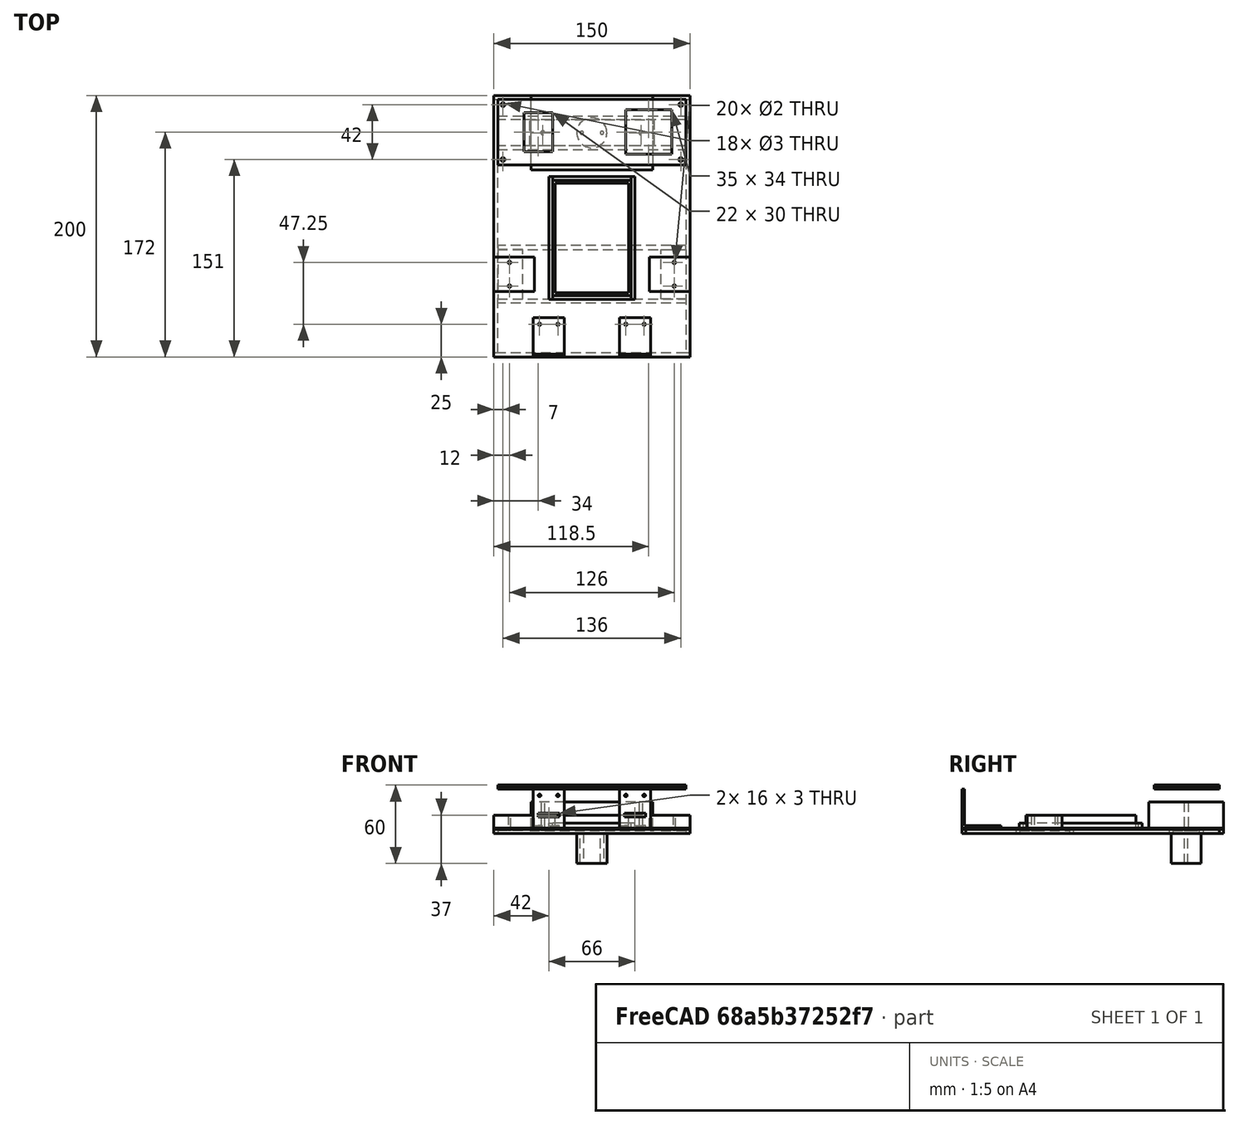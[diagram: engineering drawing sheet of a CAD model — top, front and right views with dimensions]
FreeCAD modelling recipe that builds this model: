
FCSTD DOCUMENT  (FreeCAD 0.20R27078 (Git))
Label: Robot_simple_brackets
License: All rights reserved
LicenseURL: http://en.wikipedia.org/wiki/All_rights_reserved
objects: TechDraw::DrawViewDimension×63, PartDesign::ShapeBinder×32, PartDesign::Pad×27, PartDesign::Body×25, TechDraw::DrawProjGroupItem×13, Sketcher::SketchObject×11, TechDraw::DrawProjGroup×10, PartDesign::Pocket×7, TechDraw::DrawSVGTemplate×5, TechDraw::DrawPage×5, PartDesign::Fillet×2, TechDraw::DrawViewAnnotation×2, TechDraw::DrawHatch×1, App::DocumentObjectGroup×1
note: 140 computed .brp shape members not serialized (recipe doc carries the construction recipe); baked Part::Feature solids carry a one-line shape summary decoded from their .brp

FEATURE [Sketcher::SketchObject] Sketch  label="ChassisOutline"
  FullyConstrained = true
  MapMode = 5
  Support = -> [XY_Plane]
  sketch-geometry (4):
    g0: LineSegment StartX=-75 StartY=100 StartZ=0 EndX=75 EndY=100 EndZ=0
    g1: LineSegment StartX=75 StartY=100 StartZ=0 EndX=75 EndY=-100 EndZ=0
    g2: LineSegment StartX=75 StartY=-100 StartZ=0 EndX=-75 EndY=-100 EndZ=0
    g3: LineSegment StartX=-75 StartY=-100 StartZ=0 EndX=-75 EndY=100 EndZ=0
  constraints (11):
    c: Coincident(g0,g1)
    c: Coincident(g1,g2)
    c: Coincident(g2,g3)
    c: Coincident(g3,g0)
    c: Horizontal(g0)
    c: Horizontal(g2)
    c: Vertical(g1)
    c: Vertical(g3)
    c: Distance(g0) = 150
    c: Distance(g3) = 200
    c: Symmetric(g0,g1,g-1)
FEATURE [Sketcher::SketchObject] Sketch001  label="UpperParts"
  ExternalGeometry = -> [Sketch]
  FullyConstrained = true
  MapMode = 5
  Support = -> [XY_Plane]
  sketch-geometry (24):
    g0: LineSegment StartX=-46.5 StartY=100 StartZ=0 EndX=46.5 EndY=100 EndZ=0
    g1: LineSegment StartX=46.5 StartY=100 StartZ=0 EndX=46.5 EndY=43 EndZ=0
    g2: LineSegment StartX=46.5 StartY=43 StartZ=0 EndX=-46.5 EndY=43 EndZ=0
    g3: LineSegment StartX=-46.5 StartY=43 StartZ=0 EndX=-46.5 EndY=100 EndZ=0
    g4: LineSegment StartX=-28 StartY=33 StartZ=0 EndX=28 EndY=33 EndZ=0
    g5: LineSegment StartX=28 StartY=33 StartZ=0 EndX=28 EndY=-51 EndZ=0
    g6: LineSegment StartX=28 StartY=-51 StartZ=0 EndX=-28 EndY=-51 EndZ=0
    g7: LineSegment StartX=-28 StartY=-51 StartZ=0 EndX=-28 EndY=33 EndZ=0
    g8: LineSegment StartX=-44 StartY=-50 StartZ=0 EndX=-75 EndY=-50 EndZ=0
    g9: LineSegment StartX=-75 StartY=-50 StartZ=0 EndX=-75 EndY=-23.5 EndZ=0
    g10: LineSegment StartX=-75 StartY=-23.5 StartZ=0 EndX=-44 EndY=-23.5 EndZ=0
    g11: LineSegment StartX=-44 StartY=-23.5 StartZ=0 EndX=-44 EndY=-50 EndZ=0
    g12: LineSegment StartX=75 StartY=-23.5 StartZ=0 EndX=44 EndY=-23.5 EndZ=0
    g13: LineSegment StartX=44 StartY=-23.5 StartZ=0 EndX=44 EndY=-50 EndZ=0
    g14: LineSegment StartX=44 StartY=-50 StartZ=0 EndX=75 EndY=-50 EndZ=0
    g15: LineSegment StartX=75 StartY=-50 StartZ=0 EndX=75 EndY=-23.5 EndZ=0
    g16: LineSegment StartX=-37.5 StartY=71.5 StartZ=0 EndX=0 EndY=71.5 EndZ=0
    g17: Circle CenterX=-37.5 CenterY=71.5 CenterZ=0 NormalX=0 NormalY=0 NormalZ=1 AngleXU=0 Radius=1.5
    g18: Circle CenterX=37.5 CenterY=71.5 CenterZ=0 NormalX=0 NormalY=0 NormalZ=1 AngleXU=0 Radius=1.5
    g19: Circle CenterX=-63 CenterY=-27.75 CenterZ=0 NormalX=0 NormalY=0 NormalZ=1 AngleXU=0 Radius=1
    g20: Circle CenterX=-63 CenterY=-45.75 CenterZ=0 NormalX=0 NormalY=0 NormalZ=1 AngleXU=0 Radius=1
    g21: Circle CenterX=63 CenterY=-27.75 CenterZ=0 NormalX=0 NormalY=0 NormalZ=1 AngleXU=0 Radius=1
    g22: Circle CenterX=63 CenterY=-45.75 CenterZ=0 NormalX=0 NormalY=0 NormalZ=1 AngleXU=0 Radius=1
    g23: LineSegment StartX=-75 StartY=-36.75 StartZ=0 EndX=-44 EndY=-36.75 EndZ=0
  constraints (64):
    c: Coincident(g0,g1)
    c: Coincident(g1,g2)
    c: Coincident(g2,g3)
    c: Coincident(g3,g0)
    c: Horizontal(g0)
    c: Vertical(g1)
    c: Vertical(g3)
    c: PointOnObject(g0,g-3)
    c: Symmetric(g2,g1,g-2)
    c: Distance(g2) = 93
    c: Distance(g3) = 57
    c: Coincident(g4,g5)
    c: Coincident(g5,g6)
    c: Coincident(g6,g7)
    c: Coincident(g7,g4)
    c: Horizontal(g6)
    c: Vertical(g5)
    c: Vertical(g7)
    c: Symmetric(g4,g4,g-2)
    c: Distance(g4) = 56
    c: Distance(g7) = 84
    c: DistanceY(g4,g2) = 10
    c: Coincident(g8,g9)
    c: Coincident(g9,g10)
    c: Coincident(g10,g11)
    c: Coincident(g11,g8)
    c: Horizontal(g8)
    c: Horizontal(g10)
    c: Vertical(g9)
    c: Vertical(g11)
    c: PointOnObject(g9,g-4)
    c: Coincident(g12,g13)
    c: Coincident(g13,g14)
    c: Coincident(g14,g15)
    c: Coincident(g15,g12)
    c: Horizontal(g12)
    c: Horizontal(g14)
    c: Vertical(g13)
    c: Vertical(g15)
    c: PointOnObject(g12,g-6)
    c: Symmetric(g10,g12,g-2)
    c: Equal(g11,g13)
    c: Distance(g9) = 26.5
    c: Distance(g10) = 31
    c: Distance(g8,g-5) = 50
    c: PointOnObject(g16,g-2)
    c: Coincident(g17,g16)
    c: DistanceX(g17,g18) = 75
    c: Equal(g17,g18)
    c: Symmetric(g17,g18,g-2)
    c: Diameter(g18) = 3
    c: Symmetric(g0,g2,g16)
    c: PointOnObject(g23,g9)
    c: PointOnObject(g23,g11)
    c: Symmetric(g19,g20,g23)
    c: Distance(g20,g19) = 18
    c: Symmetric(g8,g9,g23)
    c: Symmetric(g20,g22,g-2)
    c: Symmetric(g19,g21,g-2)
    c: Equal(g21,g22)
    c: Equal(g22,g20)
    c: Equal(g20,g19)
    c: Diameter(g19) = 2
    c: DistanceX(g9,g19) = 12
FEATURE [PartDesign::Pad] Pad
  Direction = (0,0,1)
  Length = 1
  Length2 = 100
  Profile = -> Sketch
  Reversed = true
  Type = 0
FEATURE [PartDesign::ShapeBinder] ShapeBinder
  Support = -> [Sketch001]
  TraceSupport = false
FEATURE [PartDesign::Pocket] Pocket
  BaseFeature = -> Pad
  Direction = (1,1,1)
  Length = 5
  Length2 = 100
  Profile = -> ShapeBinder
  Type = 1
FEATURE [PartDesign::ShapeBinder] ShapeBinder001
  Support = -> [Sketch001]
  TraceSupport = false
FEATURE [PartDesign::Pad] Pad001
  Direction = (0,0,-1)
  Length = 20
  Length2 = 100
  Profile = -> ShapeBinder001
  Reversed = true
  Type = 0
FEATURE [PartDesign::Body] Body001  label="BatteryBox"
  Group = -> [ShapeBinder001,Pad001]
  Origin = -> Origin001
  Tip = -> Pad001
FEATURE [PartDesign::ShapeBinder] ShapeBinder002
  Support = -> [Sketch001]
  TraceSupport = false
FEATURE [PartDesign::Pad] Pad002
  Direction = (0,0,-1)
  Length = 10
  Length2 = 100
  Profile = -> ShapeBinder002
  Reversed = true
  Type = 0
FEATURE [PartDesign::Body] Body002  label="Breadboard"
  Group = -> [ShapeBinder002,Pad002]
  Origin = -> Origin002
  Tip = -> Pad002
FEATURE [PartDesign::ShapeBinder] ShapeBinder003
  Support = -> [Sketch001]
  TraceSupport = false
FEATURE [PartDesign::Pad] Pad003
  Direction = (0,0,-1)
  Length = 10
  Length2 = 100
  Profile = -> ShapeBinder003
  Reversed = true
  Type = 0
FEATURE [PartDesign::Body] Body003  label="LeftMotor"
  Group = -> [ShapeBinder003,Pad003]
  Origin = -> Origin003
  Tip = -> Pad003
FEATURE [PartDesign::ShapeBinder] ShapeBinder004
  Support = -> [Sketch001]
  TraceSupport = false
FEATURE [PartDesign::Pad] Pad004
  Direction = (0,0,1)
  Length = 10
  Length2 = 100
  Profile = -> ShapeBinder004
  Type = 0
FEATURE [PartDesign::Body] Body004  label="RightMotor"
  Group = -> [ShapeBinder004,Pad004]
  Origin = -> Origin004
  Tip = -> Pad004
FEATURE [Sketcher::SketchObject] Sketch002  label="OuterSupportRods"
  ExternalGeometry = -> [Pocket]
  FullyConstrained = true
  MapMode = 5
  Placement = pos=(0,0,-1) rot=(1,0,0;3.14159rad)
  Support = -> [Pocket]
  sketch-geometry (16):
    g0: LineSegment StartX=-75 StartY=100 StartZ=0 EndX=75 EndY=100 EndZ=0
    g1: LineSegment StartX=75 StartY=100 StartZ=0 EndX=75 EndY=97 EndZ=0
    g2: LineSegment StartX=-75 StartY=97 StartZ=0 EndX=-75 EndY=100 EndZ=0
    g3: LineSegment StartX=75 StartY=-100 StartZ=0 EndX=-75 EndY=-100 EndZ=0
    g4: LineSegment StartX=-75 StartY=-100 StartZ=0 EndX=-75 EndY=-97 EndZ=0
    g5: LineSegment StartX=75 StartY=-97 StartZ=0 EndX=75 EndY=-100 EndZ=0
    g6: LineSegment StartX=-72 StartY=97 StartZ=0 EndX=-75 EndY=97 EndZ=0
    g7: LineSegment StartX=75 StartY=97 StartZ=0 EndX=72 EndY=97 EndZ=0
    g8: LineSegment StartX=72 StartY=97 StartZ=0 EndX=-72 EndY=97 EndZ=0
    g9: LineSegment StartX=72 StartY=-97 StartZ=0 EndX=75 EndY=-97 EndZ=0
    g10: LineSegment StartX=-75 StartY=-97 StartZ=0 EndX=-72 EndY=-97 EndZ=0
    g11: LineSegment StartX=-72 StartY=-97 StartZ=0 EndX=72 EndY=-97 EndZ=0
    g12: LineSegment StartX=-75 StartY=97 StartZ=0 EndX=-75 EndY=-97 EndZ=0
    g13: LineSegment StartX=75 StartY=97 StartZ=0 EndX=75 EndY=-97 EndZ=0
    g14: LineSegment StartX=72 StartY=-97 StartZ=0 EndX=72 EndY=97 EndZ=0
    g15: LineSegment StartX=-72 StartY=97 StartZ=0 EndX=-72 EndY=-97 EndZ=0
  constraints (40):
    c: Coincident(g0,g1)
    c: Coincident(g1,g7)
    c: Coincident(g6,g2)
    c: Coincident(g2,g0)
    c: Vertical(g1)
    c: Vertical(g2)
    c: Coincident(g3,g4)
    c: Coincident(g4,g10)
    c: Coincident(g9,g5)
    c: Coincident(g5,g3)
    c: Vertical(g4)
    c: Vertical(g5)
    c: Equal(g2,g4)
    c: Distance(g2) = 3
    c: Coincident(g3,g-3)
    c: Coincident(g0,g-3)
    c: Coincident(g-4,g0)
    c: Coincident(g3,g-4)
    c: Coincident(g8,g6)
    c: Horizontal(g6)
    c: Coincident(g7,g8)
    c: Horizontal(g7)
    c: Horizontal(g8)
    c: Coincident(g11,g9)
    c: Horizontal(g9)
    c: Coincident(g10,g11)
    c: Horizontal(g10)
    c: Horizontal(g11)
    c: Equal(g6,g7)
    c: Equal(g6,g2)
    c: Coincident(g12,g2)
    c: Coincident(g12,g4)
    c: Coincident(g13,g1)
    c: Coincident(g13,g5)
    c: Coincident(g14,g9)
    c: Coincident(g14,g7)
    c: Coincident(g15,g6)
    c: Coincident(g15,g10)
    c: Vertical(g15)
    c: Vertical(g14)
FEATURE [PartDesign::ShapeBinder] ShapeBinder005
  Support = -> [Sketch002]
  TraceSupport = false
FEATURE [PartDesign::Pad] Pad005
  Direction = (0,0,1)
  Length = 3
  Length2 = 100
  Profile = -> ShapeBinder005
  Reversed = true
  Type = 0
FEATURE [PartDesign::Body] Body005  label="FrontRod"
  Group = -> [ShapeBinder005,Pad005]
  Origin = -> Origin005
  Tip = -> Pad005
FEATURE [PartDesign::ShapeBinder] ShapeBinder006
  Support = -> [Sketch002]
  TraceSupport = false
FEATURE [PartDesign::Pad] Pad006
  Direction = (0,0,1)
  Length = 3
  Length2 = 100
  Profile = -> ShapeBinder006
  Reversed = true
  Type = 0
FEATURE [PartDesign::Body] Body006  label="RearRod"
  Group = -> [ShapeBinder006,Pad006]
  Origin = -> Origin006
  Tip = -> Pad006
FEATURE [PartDesign::ShapeBinder] ShapeBinder007
  Support = -> [Sketch002]
  TraceSupport = false
FEATURE [PartDesign::Pad] Pad007
  Direction = (0,0,-1)
  Length = 3
  Length2 = 100
  Profile = -> ShapeBinder007
  Type = 0
FEATURE [PartDesign::Body] Body007  label="LeftRod"
  Group = -> [ShapeBinder007,Pad007]
  Origin = -> Origin007
  Tip = -> Pad007
FEATURE [PartDesign::ShapeBinder] ShapeBinder008
  Support = -> [Sketch002]
  TraceSupport = false
FEATURE [PartDesign::Pad] Pad008
  Direction = (0,0,1)
  Length = 3
  Length2 = 100
  Profile = -> ShapeBinder008
  Reversed = true
  Type = 0
FEATURE [PartDesign::Body] Body008  label="RightRod"
  Group = -> [ShapeBinder008,Pad008]
  Origin = -> Origin008
  Tip = -> Pad008
FEATURE [Sketcher::SketchObject] Sketch003  label="InnerSupportRods"
  ExternalGeometry = -> [Sketch002,Pocket]
  FullyConstrained = true
  MapMode = 5
  Placement = pos=(0,0,-1) rot=(1,0,0;3.14159rad)
  Support = -> [Pocket]
  sketch-geometry (16):
    g0: LineSegment StartX=-72 StartY=55.75 StartZ=0 EndX=72 EndY=55.75 EndZ=0
    g1: LineSegment StartX=72 StartY=55.75 StartZ=0 EndX=72 EndY=58.75 EndZ=0
    g2: LineSegment StartX=72 StartY=58.75 StartZ=0 EndX=-72 EndY=58.75 EndZ=0
    g3: LineSegment StartX=-72 StartY=58.75 StartZ=0 EndX=-72 EndY=55.75 EndZ=0
    g4: LineSegment StartX=-72 StartY=17.75 StartZ=0 EndX=72 EndY=17.75 EndZ=0
    g5: LineSegment StartX=72 StartY=17.75 StartZ=0 EndX=72 EndY=14.75 EndZ=0
    g6: LineSegment StartX=72 StartY=14.75 StartZ=0 EndX=-72 EndY=14.75 EndZ=0
    g7: LineSegment StartX=-72 StartY=14.75 StartZ=0 EndX=-72 EndY=17.75 EndZ=0
    g8: LineSegment StartX=-72 StartY=-58.5 StartZ=0 EndX=72 EndY=-58.5 EndZ=0
    g9: LineSegment StartX=72 StartY=-58.5 StartZ=0 EndX=72 EndY=-61.5 EndZ=0
    g10: LineSegment StartX=72 StartY=-61.5 StartZ=0 EndX=-72 EndY=-61.5 EndZ=0
    g11: LineSegment StartX=-72 StartY=-61.5 StartZ=0 EndX=-72 EndY=-58.5 EndZ=0
    g12: LineSegment StartX=72 StartY=-81.5 StartZ=0 EndX=-72 EndY=-81.5 EndZ=0
    g13: LineSegment StartX=-72 StartY=-81.5 StartZ=0 EndX=-72 EndY=-84.5 EndZ=0
    g14: LineSegment StartX=-72 StartY=-84.5 StartZ=0 EndX=72 EndY=-84.5 EndZ=0
    g15: LineSegment StartX=72 StartY=-84.5 StartZ=0 EndX=72 EndY=-81.5 EndZ=0
  constraints (48):
    c: Coincident(g0,g1)
    c: Coincident(g1,g2)
    c: Coincident(g2,g3)
    c: Coincident(g3,g0)
    c: Horizontal(g0)
    c: Horizontal(g2)
    c: Vertical(g1)
    c: Vertical(g3)
    c: PointOnObject(g0,g-4)
    c: PointOnObject(g1,g-5)
    c: Coincident(g4,g5)
    c: Coincident(g5,g6)
    c: Coincident(g6,g7)
    c: Coincident(g7,g4)
    c: Horizontal(g4)
    c: Horizontal(g6)
    c: Vertical(g5)
    c: Vertical(g7)
    c: PointOnObject(g4,g-4)
    c: PointOnObject(g5,g-5)
    c: Coincident(g8,g9)
    c: Coincident(g9,g10)
    c: Coincident(g10,g11)
    c: Coincident(g11,g8)
    c: Horizontal(g8)
    c: Horizontal(g10)
    c: Vertical(g9)
    c: Vertical(g11)
    c: PointOnObject(g8,g-4)
    c: PointOnObject(g9,g-5)
    c: Coincident(g12,g13)
    c: Coincident(g13,g14)
    c: Coincident(g14,g15)
    c: Coincident(g15,g12)
    c: Horizontal(g12)
    c: Horizontal(g14)
    c: Vertical(g13)
    c: Vertical(g15)
    c: PointOnObject(g12,g-5)
    c: PointOnObject(g13,g-4)
    c: Equal(g13,g11)
    c: Equal(g11,g7)
    c: Equal(g7,g3)
    c: Equal(g3,g-3)
    c: DistanceY(g-8,g0) = 10
    c: DistanceY(g4,g-9) = 10
    c: DistanceY(g-10,g10) = 10
    c: DistanceY(g12,g-10) = 10
FEATURE [Sketcher::SketchObject] Sketch004  label="SupportPlates"
  ExternalGeometry = -> [Sketch002,Sketch003,Pocket]
  FullyConstrained = true
  MapMode = 5
  Placement = pos=(0,0,-1) rot=(1,0,0;3.14159rad)
  Support = -> [Pocket]
  sketch-geometry (18):
    g0: Circle CenterX=-63 CenterY=45.75 CenterZ=0 NormalX=0 NormalY=0 NormalZ=1 AngleXU=0 Radius=1
    g1: Circle CenterX=-63 CenterY=27.75 CenterZ=0 NormalX=0 NormalY=0 NormalZ=1 AngleXU=0 Radius=1
    g2: Circle CenterX=63 CenterY=45.75 CenterZ=0 NormalX=0 NormalY=0 NormalZ=1 AngleXU=0 Radius=1
    g3: Circle CenterX=63 CenterY=27.75 CenterZ=0 NormalX=0 NormalY=0 NormalZ=1 AngleXU=0 Radius=1
    g4: Circle CenterX=-37.5 CenterY=-71.5 CenterZ=0 NormalX=0 NormalY=0 NormalZ=1 AngleXU=0 Radius=1.5
    g5: Circle CenterX=37.5 CenterY=-71.5 CenterZ=0 NormalX=0 NormalY=0 NormalZ=1 AngleXU=0 Radius=1.5
    g6: LineSegment StartX=-72 StartY=55.75 StartZ=0 EndX=-53 EndY=55.75 EndZ=0
    g7: LineSegment StartX=-53 StartY=55.75 StartZ=0 EndX=-53 EndY=17.75 EndZ=0
    g8: LineSegment StartX=-53 StartY=17.75 StartZ=0 EndX=-72 EndY=17.75 EndZ=0
    g9: LineSegment StartX=-72 StartY=17.75 StartZ=0 EndX=-72 EndY=55.75 EndZ=0
    g10: LineSegment StartX=72 StartY=55.75 StartZ=0 EndX=53 EndY=55.75 EndZ=0
    g11: LineSegment StartX=53 StartY=55.75 StartZ=0 EndX=53 EndY=17.75 EndZ=0
    g12: LineSegment StartX=53 StartY=17.75 StartZ=0 EndX=72 EndY=17.75 EndZ=0
    g13: LineSegment StartX=72 StartY=17.75 StartZ=0 EndX=72 EndY=55.75 EndZ=0
    g14: LineSegment StartX=47.5 StartY=-61.5 StartZ=0 EndX=-47.5 EndY=-61.5 EndZ=0
    g15: LineSegment StartX=-47.5 StartY=-61.5 StartZ=0 EndX=-47.5 EndY=-81.5 EndZ=0
    g16: LineSegment StartX=-47.5 StartY=-81.5 StartZ=0 EndX=47.5 EndY=-81.5 EndZ=0
    g17: LineSegment StartX=47.5 StartY=-81.5 StartZ=0 EndX=47.5 EndY=-61.5 EndZ=0
  constraints (44):
    c: Coincident(g0,g-9)
    c: Coincident(g1,g-10)
    c: Coincident(g2,g-7)
    c: Coincident(g3,g-8)
    c: Coincident(g4,g-13)
    c: Coincident(g5,g-14)
    c: Equal(g-10,g1)
    c: Equal(g0,g-9)
    c: Equal(g2,g-7)
    c: Equal(g3,g-8)
    c: Equal(g5,g-14)
    c: Equal(g4,g-13)
    c: Coincident(g6,g7)
    c: Coincident(g7,g8)
    c: Coincident(g8,g9)
    c: Coincident(g9,g6)
    c: Horizontal(g6)
    c: Horizontal(g8)
    c: Vertical(g7)
    c: Vertical(g9)
    c: Coincident(g6,g-5)
    c: PointOnObject(g7,g-6)
    c: Coincident(g10,g11)
    c: Coincident(g11,g12)
    c: Coincident(g12,g13)
    c: Coincident(g13,g10)
    c: Horizontal(g12)
    c: Vertical(g11)
    c: Vertical(g13)
    c: Coincident(g10,g-5)
    c: PointOnObject(g11,g-6)
    c: Coincident(g14,g15)
    c: Coincident(g15,g16)
    c: Coincident(g16,g17)
    c: Coincident(g17,g14)
    c: Horizontal(g16)
    c: Vertical(g15)
    c: Vertical(g17)
    c: PointOnObject(g14,g-11)
    c: PointOnObject(g15,g-12)
    c: Symmetric(g6,g10,g-2)
    c: Symmetric(g14,g14,g-2)
    c: DistanceX(g0,g6) = 10
    c: DistanceX(g14,g4) = 10
FEATURE [PartDesign::ShapeBinder] ShapeBinder009
  Support = -> [Sketch003]
  TraceSupport = false
FEATURE [PartDesign::Pad] Pad009
  Direction = (0,0,-1)
  Length = 3
  Length2 = 100
  Profile = -> ShapeBinder009
  Type = 0
FEATURE [PartDesign::Body] Body009  label="MotorFrontRod"
  Group = -> [ShapeBinder009,Pad009]
  Origin = -> Origin009
  Tip = -> Pad009
FEATURE [PartDesign::ShapeBinder] ShapeBinder010
  Support = -> [Sketch003]
  TraceSupport = false
FEATURE [PartDesign::Pad] Pad010
  Direction = (0,0,-1)
  Length = 3
  Length2 = 100
  Profile = -> ShapeBinder010
  Type = 0
FEATURE [PartDesign::Body] Body010  label="BatteryRearRod"
  Group = -> [ShapeBinder010,Pad010]
  Origin = -> Origin010
  Tip = -> Pad010
FEATURE [PartDesign::ShapeBinder] ShapeBinder011
  Support = -> [Sketch003]
  TraceSupport = false
FEATURE [PartDesign::Pad] Pad011
  Direction = (0,0,1)
  Length = 3
  Length2 = 100
  Profile = -> ShapeBinder011
  Reversed = true
  Type = 0
FEATURE [PartDesign::Body] Body011  label="BatteryFrontRod"
  Group = -> [ShapeBinder011,Pad011]
  Origin = -> Origin011
  Tip = -> Pad011
FEATURE [PartDesign::ShapeBinder] ShapeBinder012
  Support = -> [Sketch003]
  TraceSupport = false
FEATURE [PartDesign::Pad] Pad012
  Direction = (0,0,1)
  Length = 3
  Length2 = 100
  Profile = -> ShapeBinder012
  Reversed = true
  Type = 0
FEATURE [PartDesign::Body] Body012  label="MotorRearRod"
  Group = -> [ShapeBinder012,Pad012]
  Origin = -> Origin012
  Tip = -> Pad012
FEATURE [PartDesign::ShapeBinder] ShapeBinder013
  Support = -> [Sketch004]
  TraceSupport = false
FEATURE [PartDesign::Pad] Pad013
  Direction = (0,0,-1)
  Length = 1
  Length2 = 100
  Profile = -> ShapeBinder013
  Type = 0
FEATURE [PartDesign::ShapeBinder] ShapeBinder014
  Support = -> [Sketch004]
  TraceSupport = false
FEATURE [PartDesign::Pad] Pad014
  Direction = (0,0,-1)
  Length = 1
  Length2 = 100
  Profile = -> ShapeBinder014
  Type = 0
FEATURE [PartDesign::Body] Body014  label="RightMotorPlate"
  Group = -> [ShapeBinder014,Pad014]
  Origin = -> Origin014
  Tip = -> Pad014
FEATURE [PartDesign::ShapeBinder] ShapeBinder015
  Support = -> [Sketch004]
  TraceSupport = false
FEATURE [PartDesign::Pad] Pad015
  Direction = (0,0,1)
  Length = 1
  Length2 = 100
  Profile = -> ShapeBinder015
  Reversed = true
  Type = 0
FEATURE [PartDesign::Body] Body015  label="LeftMotorPlate"
  Group = -> [ShapeBinder015,Pad015]
  Origin = -> Origin015
  Tip = -> Pad015
FEATURE [Sketcher::SketchObject] Sketch005  label="CastorSketch"
  ExternalGeometry = -> [Pocket]
  FullyConstrained = true
  MapMode = 5
  Placement = pos=(0,0,-1) rot=(1,0,0;3.14159rad)
  Support = -> [Pocket]
  sketch-geometry (4):
    g0: LineSegment StartX=-37.5 StartY=-71.5 StartZ=0 EndX=0 EndY=-71.5 EndZ=0
    g1: Circle CenterX=-7.75 CenterY=-71.5 CenterZ=0 NormalX=0 NormalY=0 NormalZ=1 AngleXU=0 Radius=1.25
    g2: Circle CenterX=7.75 CenterY=-71.5 CenterZ=0 NormalX=0 NormalY=0 NormalZ=1 AngleXU=0 Radius=1.25
    g3: Circle CenterX=0 CenterY=-71.5 CenterZ=0 NormalX=0 NormalY=0 NormalZ=1 AngleXU=0 Radius=11.5
  constraints (10):
    c: Coincident(g0,g-3)
    c: PointOnObject(g0,g-2)
    c: Horizontal(g0)
    c: PointOnObject(g1,g0)
    c: Equal(g1,g2)
    c: Symmetric(g1,g2,g-2)
    c: Distance(g1,g2) = 15.5
    c: Diameter(g1) = 2.5
    c: Coincident(g3,g0)
    c: Diameter(g3) = 23
FEATURE [PartDesign::ShapeBinder] ShapeBinder016
  Support = -> [Sketch005]
  TraceSupport = false
FEATURE [PartDesign::Pocket] Pocket001
  BaseFeature = -> Pocket
  Direction = (1,1,1)
  Length = 5
  Length2 = 100
  Profile = -> ShapeBinder016
  Reversed = true
  Type = 1
FEATURE [PartDesign::ShapeBinder] ShapeBinder017
  Support = -> [Sketch005]
  TraceSupport = false
FEATURE [PartDesign::Pocket] Pocket002
  BaseFeature = -> Pad013
  Direction = (1,1,1)
  Length = 5
  Length2 = 100
  Profile = -> ShapeBinder017
  Type = 1
FEATURE [PartDesign::Body] Body013  label="BatteryPlate"
  Group = -> [ShapeBinder013,Pad013,ShapeBinder017,Pocket002]
  Origin = -> Origin013
  Tip = -> Pocket002
FEATURE [PartDesign::ShapeBinder] ShapeBinder018
  Support = -> [Sketch005]
  TraceSupport = false
FEATURE [PartDesign::Pad] Pad016
  Direction = (0,0,-1)
  Length = 23
  Length2 = 100
  Profile = -> ShapeBinder018
  Type = 0
FEATURE [PartDesign::Body] Body016  label="Castor"
  Group = -> [ShapeBinder018,Pad016]
  Origin = -> Origin016
  Placement = pos=(0,0,-3) rot=(0,0,1;0rad)
  Tip = -> Pad016
FEATURE [TechDraw::DrawSVGTemplate] Template003  label="Template"
  Height = 297
  Orientation = 0
  Width = 210
FEATURE [TechDraw::DrawProjGroupItem] ProjItem007  label="Front002"
  CoarseView = false
  Direction = (0,0,-1)
  Focus = 100
  HardHidden = false
  IsoCount = 0
  IsoHidden = false
  IsoVisible = false
  LockPosition = true
  Perspective = false
  Rotation = 0
  RotationVector = (1,0,0)
  ScaleType = 2
  SeamHidden = false
  SeamVisible = true
  SmoothHidden = false
  SmoothVisible = true
  Source = -> [Body013]
  Type = 0
  X = 0
  XDirection = (1e-16,1,0)
  Y = 0
FEATURE [TechDraw::DrawProjGroup] ProjGroup007  label="ProjGroup002"
  Anchor = -> ProjItem007
  AutoDistribute = true
  LockPosition = false
  ProjectionType = 0
  Rotation = 0
  ScaleType = 0
  Source = -> [Body013]
  Views = -> [ProjItem007]
  X = 28.3326
  Y = 235.758
  spacingX = 15
  spacingY = 15
FEATURE [TechDraw::DrawProjGroupItem] ProjItem008  label="Front003"
  CoarseView = false
  Direction = (0,0,-1)
  Focus = 100
  HardHidden = false
  IsoCount = 0
  IsoHidden = false
  IsoVisible = false
  LockPosition = true
  Perspective = false
  Rotation = 0
  RotationVector = (1,0,0)
  ScaleType = 2
  SeamHidden = false
  SeamVisible = true
  SmoothHidden = false
  SmoothVisible = true
  Source = -> [Body014]
  Type = 0
  X = 0
  XDirection = (1,0,0)
  Y = 0
FEATURE [TechDraw::DrawProjGroup] ProjGroup008  label="ProjGroup003"
  Anchor = -> ProjItem008
  AutoDistribute = true
  LockPosition = false
  ProjectionType = 0
  Rotation = 0
  ScaleType = 0
  Source = -> [Body014]
  Views = -> [ProjItem008]
  X = 28.3326
  Y = 156.788
  spacingX = 15
  spacingY = 15
FEATURE [TechDraw::DrawProjGroupItem] ProjItem009  label="Front004"
  CoarseView = false
  Direction = (0,0,-1)
  Focus = 100
  HardHidden = false
  IsoCount = 0
  IsoHidden = false
  IsoVisible = false
  LockPosition = true
  Perspective = false
  Rotation = 0
  RotationVector = (1,0,0)
  ScaleType = 2
  SeamHidden = false
  SeamVisible = true
  SmoothHidden = false
  SmoothVisible = true
  Source = -> [Body015]
  Type = 0
  X = 0
  XDirection = (1,0,0)
  Y = 0
FEATURE [TechDraw::DrawProjGroup] ProjGroup009  label="ProjGroup004"
  Anchor = -> ProjItem009
  AutoDistribute = true
  LockPosition = false
  ProjectionType = 0
  Rotation = 0
  ScaleType = 0
  Source = -> [Body015]
  Views = -> [ProjItem009]
  X = 28.5628
  Y = 104.526
  spacingX = 15
  spacingY = 15
FEATURE [TechDraw::DrawViewDimension] Dimension017
  Arbitrary = false
  ArbitraryTolerances = false
  EqualTolerance = true
  FormatSpec = ⌀%.2f
  FormatSpecOverTolerance = %+.2f
  FormatSpecUnderTolerance = %+.2f
  Inverted = false
  LockPosition = false
  MeasureType = 1
  OverTolerance = 0
  References2D = -> [ProjItem007]
  Rotation = 0
  ScaleType = 0
  TheoreticalExact = false
  Type = 5
  UnderTolerance = 0
  X = 6.56075
  Y = -24.9813
FEATURE [TechDraw::DrawViewDimension] Dimension018
  Arbitrary = false
  ArbitraryTolerances = false
  EqualTolerance = true
  FormatSpec = ⌀%.2f
  FormatSpecOverTolerance = %+.2f
  FormatSpecUnderTolerance = %+.2f
  Inverted = false
  LockPosition = false
  MeasureType = 1
  OverTolerance = 0
  References2D = -> [ProjItem007]
  Rotation = 0
  ScaleType = 0
  TheoreticalExact = false
  Type = 5
  UnderTolerance = 0
  X = 10.5981
  Y = 1.76635
FEATURE [TechDraw::DrawViewDimension] Dimension019
  Arbitrary = false
  ArbitraryTolerances = false
  EqualTolerance = true
  FormatSpec = ⌀%.2f
  FormatSpecOverTolerance = %+.2f
  FormatSpecUnderTolerance = %+.2f
  Inverted = false
  LockPosition = false
  MeasureType = 1
  OverTolerance = 0
  References2D = -> [ProjItem009]
  Rotation = 0
  ScaleType = 0
  TheoreticalExact = false
  Type = 5
  UnderTolerance = 0
  X = 13.2772
  Y = 17.7562
FEATURE [TechDraw::DrawViewDimension] Dimension020
  Arbitrary = false
  ArbitraryTolerances = false
  EqualTolerance = true
  FormatSpec = ⌀%.2f
  FormatSpecOverTolerance = %+.2f
  FormatSpecUnderTolerance = %+.2f
  Inverted = false
  LockPosition = false
  MeasureType = 1
  OverTolerance = 0
  References2D = -> [ProjItem008]
  Rotation = 0
  ScaleType = 0
  TheoreticalExact = false
  Type = 5
  UnderTolerance = 0
  X = 6.25558
  Y = 24.4054
FEATURE [Sketcher::SketchObject] Sketch006  label="BreadboardHolder"
  ExternalGeometry = -> [Sketch001]
  FullyConstrained = true
  MapMode = 5
  Support = -> [XY_Plane]
  sketch-geometry (16):
    g0: LineSegment StartX=-30 StartY=35 StartZ=0 EndX=30 EndY=35 EndZ=0
    g1: LineSegment StartX=30 StartY=35 StartZ=0 EndX=30 EndY=-53 EndZ=0
    g2: LineSegment StartX=30 StartY=-53 StartZ=0 EndX=-30 EndY=-53 EndZ=0
    g3: LineSegment StartX=-30 StartY=-53 StartZ=0 EndX=-30 EndY=35 EndZ=0
    g4: LineSegment StartX=33 StartY=38 StartZ=0 EndX=33 EndY=-56 EndZ=0
    g5: LineSegment StartX=-33 StartY=-56 StartZ=0 EndX=-33 EndY=38 EndZ=0
    g6: LineSegment StartX=-30 StartY=35 StartZ=0 EndX=-30 EndY=38 EndZ=0
    g7: LineSegment StartX=30 StartY=35 StartZ=0 EndX=30 EndY=38 EndZ=0
    g8: LineSegment StartX=-30 StartY=-53 StartZ=0 EndX=-30 EndY=-56 EndZ=0
    g9: LineSegment StartX=30 StartY=-53 StartZ=0 EndX=30 EndY=-56 EndZ=0
    g10: LineSegment StartX=-33 StartY=38 StartZ=0 EndX=-30 EndY=38 EndZ=0
    g11: LineSegment StartX=-30 StartY=38 StartZ=0 EndX=30 EndY=38 EndZ=0
    g12: LineSegment StartX=30 StartY=38 StartZ=0 EndX=33 EndY=38 EndZ=0
    g13: LineSegment StartX=33 StartY=-56 StartZ=0 EndX=30 EndY=-56 EndZ=0
    g14: LineSegment StartX=30 StartY=-56 StartZ=0 EndX=-30 EndY=-56 EndZ=0
    g15: LineSegment StartX=-30 StartY=-56 StartZ=0 EndX=-33 EndY=-56 EndZ=0
  constraints (39):
    c: Coincident(g0,g1)
    c: Coincident(g1,g2)
    c: Coincident(g2,g3)
    c: Coincident(g3,g0)
    c: Horizontal(g2)
    c: Vertical(g1)
    c: Vertical(g3)
    c: DistanceX(g-4,g0) = 2
    c: DistanceY(g-4,g0) = 2
    c: Symmetric(g0,g0,g-2)
    c: DistanceY(g1,g-5) = 2
    c: Coincident(g12,g4)
    c: Coincident(g4,g13)
    c: Coincident(g15,g5)
    c: Coincident(g5,g10)
    c: Vertical(g4)
    c: Vertical(g5)
    c: Symmetric(g12,g10,g-2)
    c: DistanceX(g0,g12) = 3
    c: DistanceY(g0,g12) = 3
    c: DistanceY(g4,g1) = 3
    c: Coincident(g6,g0)
    c: Vertical(g6)
    c: Coincident(g7,g0)
    c: Vertical(g7)
    c: Coincident(g8,g2)
    c: Vertical(g8)
    c: Coincident(g9,g1)
    c: Vertical(g9)
    c: Tangent(g11,g12) = -1.5708
    c: Tangent(g10,g11) = -1.5708
    c: Coincident(g6,g10)
    c: Coincident(g11,g7)
    c: Coincident(g13,g14)
    c: Horizontal(g13)
    c: Coincident(g13,g9)
    c: Horizontal(g14)
    c: Tangent(g14,g15) = -1.5708
    c: Coincident(g14,g8)
FEATURE [PartDesign::ShapeBinder] ShapeBinder019
  Support = -> [Sketch006]
  TraceSupport = false
FEATURE [PartDesign::Pad] Pad017
  Direction = (0,0,-1)
  Length = 4
  Length2 = 100
  Profile = -> ShapeBinder019
  Reversed = true
  Type = 0
FEATURE [PartDesign::Body] Body017  label="BreadboardRightRod"
  Group = -> [ShapeBinder019,Pad017]
  Origin = -> Origin017
  Tip = -> Pad017
FEATURE [PartDesign::ShapeBinder] ShapeBinder020
  Support = -> [Sketch006]
  TraceSupport = false
FEATURE [PartDesign::Pad] Pad018
  Direction = (0,0,-1)
  Length = 4
  Length2 = 100
  Profile = -> ShapeBinder020
  Reversed = true
  Type = 0
FEATURE [PartDesign::Body] Body018  label="BreadboardFrontRod"
  Group = -> [ShapeBinder020,Pad018]
  Origin = -> Origin018
  Tip = -> Pad018
FEATURE [PartDesign::ShapeBinder] ShapeBinder021
  Support = -> [Sketch006]
  TraceSupport = false
FEATURE [PartDesign::Pad] Pad019
  Direction = (0,0,1)
  Length = 4
  Length2 = 100
  Profile = -> ShapeBinder021
  Type = 0
FEATURE [PartDesign::Body] Body019  label="BreadboardLeftRod"
  Group = -> [ShapeBinder021,Pad019]
  Origin = -> Origin019
  Tip = -> Pad019
FEATURE [PartDesign::ShapeBinder] ShapeBinder022
  Support = -> [Sketch006]
  TraceSupport = false
FEATURE [PartDesign::Pad] Pad020
  Direction = (0,0,1)
  Length = 4
  Length2 = 100
  Profile = -> ShapeBinder022
  Type = 0
FEATURE [PartDesign::Body] Body020  label="BreadboardRearRod"
  Group = -> [ShapeBinder022,Pad020]
  Origin = -> Origin020
  Tip = -> Pad020
FEATURE [TechDraw::DrawSVGTemplate] Template  label="Template001"
  Height = 297
  Orientation = 0
  Width = 210
FEATURE [Sketcher::SketchObject] Sketch007  label="UpperPlate"
  ExternalGeometry = -> [Sketch002]
  FullyConstrained = true
  MapMode = 5
  Support = -> [XY_Plane]
  sketch-geometry (25):
    g0: LineSegment StartX=-51 StartY=86 StartZ=0 EndX=-31 EndY=86 EndZ=0
    g1: LineSegment StartX=-31 StartY=86 StartZ=0 EndX=-31 EndY=58 EndZ=0
    g2: LineSegment StartX=-31 StartY=58 StartZ=0 EndX=-51 EndY=58 EndZ=0
    g3: LineSegment StartX=-51 StartY=58 StartZ=0 EndX=-51 EndY=86 EndZ=0
    g4: LineSegment StartX=27 StartY=88 StartZ=0 EndX=60 EndY=88 EndZ=0
    g5: LineSegment StartX=60 StartY=88 StartZ=0 EndX=60 EndY=56 EndZ=0
    g6: LineSegment StartX=60 StartY=56 StartZ=0 EndX=27 EndY=56 EndZ=0
    g7: LineSegment StartX=27 StartY=56 StartZ=0 EndX=27 EndY=88 EndZ=0
    g8: LineSegment StartX=-72 StartY=97 StartZ=0 EndX=72 EndY=97 EndZ=0
    g9: LineSegment StartX=72 StartY=97 StartZ=0 EndX=72 EndY=47 EndZ=0
    g10: LineSegment StartX=72 StartY=47 StartZ=0 EndX=-72 EndY=47 EndZ=0
    g11: LineSegment StartX=-72 StartY=47 StartZ=0 EndX=-72 EndY=97 EndZ=0
    g12: Circle CenterX=-68 CenterY=93 CenterZ=0 NormalX=0 NormalY=0 NormalZ=1 AngleXU=0 Radius=1.5
    g13: Circle CenterX=-68 CenterY=51 CenterZ=0 NormalX=0 NormalY=0 NormalZ=1 AngleXU=0 Radius=1.5
    g14: Circle CenterX=68 CenterY=51 CenterZ=0 NormalX=0 NormalY=0 NormalZ=1 AngleXU=0 Radius=1.5
    g15: Circle CenterX=68 CenterY=93 CenterZ=0 NormalX=0 NormalY=0 NormalZ=1 AngleXU=0 Radius=1.5
    g16: LineSegment StartX=-52 StartY=87 StartZ=0 EndX=-30 EndY=87 EndZ=0
    g17: LineSegment StartX=-30 StartY=87 StartZ=0 EndX=-30 EndY=57 EndZ=0
    g18: LineSegment StartX=-30 StartY=57 StartZ=0 EndX=-52 EndY=57 EndZ=0
    g19: LineSegment StartX=-52 StartY=57 StartZ=0 EndX=-52 EndY=87 EndZ=0
    g20: LineSegment StartX=26 StartY=89 StartZ=0 EndX=61 EndY=89 EndZ=0
    g21: LineSegment StartX=61 StartY=89 StartZ=0 EndX=61 EndY=55 EndZ=0
    g22: LineSegment StartX=61 StartY=55 StartZ=0 EndX=26 EndY=55 EndZ=0
    g23: LineSegment StartX=26 StartY=55 StartZ=0 EndX=26 EndY=89 EndZ=0
    g24: LineSegment StartX=-72 StartY=72 StartZ=0 EndX=72 EndY=72 EndZ=0
  constraints (66):
    c: Coincident(g0,g1)
    c: Coincident(g1,g2)
    c: Coincident(g2,g3)
    c: Coincident(g3,g0)
    c: Horizontal(g0)
    c: Horizontal(g2)
    c: Vertical(g1)
    c: Vertical(g3)
    c: Coincident(g4,g5)
    c: Coincident(g5,g6)
    c: Coincident(g6,g7)
    c: Coincident(g7,g4)
    c: Horizontal(g4)
    c: Horizontal(g6)
    c: Vertical(g5)
    c: Vertical(g7)
    c: DistanceX(g0,g0) = 20
    c: DistanceY(g1,g1) = 28
    c: DistanceY(g5,g5) = 32
    c: DistanceX(g4,g4) = 33
    c: Coincident(g8,g9)
    c: Coincident(g9,g10)
    c: Coincident(g10,g11)
    c: Coincident(g11,g8)
    c: Horizontal(g10)
    c: Equal(g15,g14)
    c: Equal(g14,g13)
    c: Equal(g13,g12)
    c: Symmetric(g12,g15,g-2)
    c: Symmetric(g13,g14,g-2)
    c: Coincident(g8,g-5)
    c: Coincident(g8,g-4)
    c: Coincident(g16,g17)
    c: Coincident(g17,g18)
    c: Coincident(g18,g19)
    c: Coincident(g19,g16)
    c: Horizontal(g16)
    c: Horizontal(g18)
    c: Vertical(g17)
    c: Coincident(g20,g21)
    c: Coincident(g21,g22)
    c: Coincident(g22,g23)
    c: Coincident(g23,g20)
    c: Horizontal(g20)
    c: Horizontal(g22)
    c: Vertical(g21)
    c: DistanceY(g4,g20) = 1
    c: DistanceX(g20,g4) = 1
    c: DistanceY(g22,g6) = 1
    c: DistanceX(g4,g20) = 1
    c: DistanceX(g16,g0) = 1
    c: DistanceY(g0,g16) = 1
    c: DistanceX(g0,g16) = 1
    c: DistanceY(g18,g2) = 1
    c: DistanceY(g11,g11) = 50
    c: DistanceY(g10,g13) = 4
    c: DistanceX(g10,g13) = 4
    c: Symmetric(g24,g24,g-2)
    c: Symmetric(g10,g8,g24)
    c: Symmetric(g16,g18,g24)
    c: Symmetric(g20,g22,g24)
    c: Symmetric(g12,g13,g24)
    c: Diameter(g13) = 3
    c: DistanceX(g16,g-1) = 30
    c: DistanceX(g-1,g22) = 26
    c: Perpendicular(g24,g9) = 4.71239
FEATURE [PartDesign::ShapeBinder] ShapeBinder025
  Support = -> [Sketch007]
  TraceSupport = false
FEATURE [PartDesign::Pocket] Pocket003
  BaseFeature = -> Pocket001
  Direction = (0,0,-1)
  Length = 5
  Length2 = 100
  Profile = -> ShapeBinder025
  Type = 1
FEATURE [Sketcher::SketchObject] Sketch008  label="SensorBracketSketch"
  ExternalGeometry = -> [Sketch003,Sketch002]
  FullyConstrained = true
  MapMode = 5
  Support = -> [XY_Plane]
  sketch-geometry (20):
    g0: LineSegment StartX=-45 StartY=-100 StartZ=0 EndX=-21 EndY=-100 EndZ=0
    g1: LineSegment StartX=21 StartY=-100 StartZ=0 EndX=45 EndY=-100 EndZ=0
    g2: LineSegment StartX=-45 StartY=-70 StartZ=0 EndX=-21 EndY=-70 EndZ=0
    g3: LineSegment StartX=21 StartY=-70 StartZ=0 EndX=45 EndY=-70 EndZ=0
    g4: Circle CenterX=-40 CenterY=-75 CenterZ=0 NormalX=0 NormalY=0 NormalZ=1 AngleXU=0 Radius=1
    g5: Circle CenterX=-26 CenterY=-75 CenterZ=0 NormalX=0 NormalY=0 NormalZ=1 AngleXU=0 Radius=1
    g6: Circle CenterX=26 CenterY=-75 CenterZ=0 NormalX=0 NormalY=0 NormalZ=1 AngleXU=0 Radius=1
    g7: Circle CenterX=40 CenterY=-75 CenterZ=0 NormalX=0 NormalY=0 NormalZ=1 AngleXU=0 Radius=1
    g8: LineSegment StartX=-33 StartY=-70 StartZ=0 EndX=-33 EndY=-100 EndZ=0
    g9: LineSegment StartX=33 StartY=-70 StartZ=0 EndX=33 EndY=-100 EndZ=0
    g10: LineSegment StartX=21 StartY=-98 StartZ=0 EndX=45 EndY=-98 EndZ=0
    g11: LineSegment StartX=21 StartY=-100 StartZ=0 EndX=21 EndY=-98 EndZ=0
    g12: LineSegment StartX=21 StartY=-98 StartZ=0 EndX=21 EndY=-70 EndZ=0
    g13: LineSegment StartX=45 StartY=-70 StartZ=0 EndX=45 EndY=-98 EndZ=0
    g14: LineSegment StartX=45 StartY=-98 StartZ=0 EndX=45 EndY=-100 EndZ=0
    g15: LineSegment StartX=-45 StartY=-98 StartZ=0 EndX=-21 EndY=-98 EndZ=0
    g16: LineSegment StartX=-45 StartY=-100 StartZ=0 EndX=-45 EndY=-98 EndZ=0
    g17: LineSegment StartX=-45 StartY=-98 StartZ=0 EndX=-45 EndY=-70 EndZ=0
    g18: LineSegment StartX=-21 StartY=-70 StartZ=0 EndX=-21 EndY=-98 EndZ=0
    g19: LineSegment StartX=-21 StartY=-98 StartZ=0 EndX=-21 EndY=-100 EndZ=0
  constraints (52):
    c: Coincident(g16,g0)
    c: Coincident(g2,g17)
    c: Coincident(g19,g0)
    c: Coincident(g11,g1)
    c: Coincident(g3,g12)
    c: Coincident(g13,g3)
    c: Coincident(g14,g1)
    c: Coincident(g2,g18)
    c: Symmetric(g17,g3,g-2)
    c: Symmetric(g12,g2,g-2)
    c: Distance(g2) = 24
    c: Equal(g7,g6)
    c: Equal(g6,g5)
    c: Equal(g5,g4)
    c: Diameter(g4) = 2
    c: PointOnObject(g8,g2)
    c: PointOnObject(g8,g0)
    c: PointOnObject(g9,g3)
    c: PointOnObject(g9,g1)
    c: Symmetric(g7,g6,g9)
    c: Symmetric(g5,g4,g8)
    c: Symmetric(g0,g0,g8)
    c: Symmetric(g1,g1,g9)
    c: Distance(g10,g1) = 2
    c: Parallel(g10,g1)
    c: Coincident(g11,g12)
    c: Perpendicular(g1,g11)
    c: Perpendicular(g1,g12)
    c: Perpendicular(g11,g3)
    c: Distance(g11,g12) = 30
    c: Coincident(g11,g10)
    c: Coincident(g13,g14)
    c: Perpendicular(g1,g13)
    c: Perpendicular(g1,g14)
    c: Coincident(g13,g10)
    c: Distance(g15,g0) = 2
    c: Parallel(g15,g0)
    c: Coincident(g16,g17)
    c: Coincident(g16,g15)
    c: Coincident(g18,g19)
    c: Perpendicular(g2,g18)
    c: Parallel(g16,g18)
    c: Parallel(g16,g19)
    c: Parallel(g17,g18)
    c: Coincident(g18,g15)
    c: Equal(g18,g12)
    c: DistanceX(g5,g6) = 52
    c: Tangent(g0,g-7)
    c: Vertical(g17)
    c: Symmetric(g5,g6,g-2)
    c: DistanceX(g4,g5) = 14
    c: DistanceY(g5,g2) = 5
FEATURE [PartDesign::ShapeBinder] ShapeBinder026
  Support = -> [Sketch008]
  TraceSupport = false
FEATURE [PartDesign::Pad] Pad023
  Direction = (0,0,-1)
  Length = 2
  Length2 = 100
  Profile = -> ShapeBinder026
  Reversed = true
  Type = 0
FEATURE [PartDesign::ShapeBinder] ShapeBinder027
  Support = -> [Sketch008]
  TraceSupport = false
FEATURE [PartDesign::Pad] Pad024
  BaseFeature = -> Pad023
  Direction = (0,0,1)
  Length = 30
  Length2 = 100
  Profile = -> ShapeBinder027
  Type = 0
FEATURE [PartDesign::Fillet] Fillet
  Base = -> Pad024 [Edge6]
  BaseFeature = -> Pad024
  Radius = 1
  SupportTransform = false
FEATURE [PartDesign::ShapeBinder] ShapeBinder028
  Support = -> [Sketch008]
  TraceSupport = false
FEATURE [PartDesign::Pad] Pad025
  Direction = (0,0,-1)
  Length = 2
  Length2 = 100
  Profile = -> ShapeBinder028
  Reversed = true
  Type = 0
FEATURE [PartDesign::ShapeBinder] ShapeBinder029
  Support = -> [Sketch008]
  TraceSupport = false
FEATURE [PartDesign::Pad] Pad026
  BaseFeature = -> Pad025
  Direction = (0,0,1)
  Length = 30
  Length2 = 100
  Profile = -> ShapeBinder029
  Type = 0
FEATURE [PartDesign::Fillet] Fillet001
  Base = -> Pad026 [Edge21]
  BaseFeature = -> Pad026
  Radius = 1
  SupportTransform = false
FEATURE [Sketcher::SketchObject] Sketch010
  ExternalGeometry = -> [Fillet001]
  FullyConstrained = true
  MapMode = 5
  Placement = pos=(0,-100,0) rot=(1,0,0;1.5708rad)
  Support = -> [Fillet001]
  sketch-geometry (7):
    g0: LineSegment StartX=33 StartY=30 StartZ=0 EndX=33 EndY=1 EndZ=0
    g1: Circle CenterX=26 CenterY=25 CenterZ=0 NormalX=0 NormalY=0 NormalZ=1 AngleXU=0 Radius=1
    g2: Circle CenterX=40 CenterY=25 CenterZ=0 NormalX=0 NormalY=0 NormalZ=1 AngleXU=0 Radius=1
    g3: LineSegment StartX=25 StartY=11.5 StartZ=0 EndX=41 EndY=11.5 EndZ=0
    g4: LineSegment StartX=41 StartY=11.5 StartZ=0 EndX=41 EndY=8.5 EndZ=0
    g5: LineSegment StartX=41 StartY=8.5 StartZ=0 EndX=25 EndY=8.5 EndZ=0
    g6: LineSegment StartX=25 StartY=8.5 StartZ=0 EndX=25 EndY=11.5 EndZ=0
  constraints (19):
    c: PointOnObject(g0,g-3)
    c: PointOnObject(g0,g-6)
    c: Symmetric(g-5,g-4,g0)
    c: Symmetric(g2,g1,g0)
    c: Diameter(g2) = 2
    c: Equal(g2,g1)
    c: DistanceX(g1,g2) = 14
    c: Coincident(g3,g4)
    c: Coincident(g4,g5)
    c: Coincident(g5,g6)
    c: Coincident(g6,g3)
    c: Horizontal(g5)
    c: Vertical(g4)
    c: Vertical(g6)
    c: DistanceY(g4,g4) = 3
    c: DistanceX(g3,g3) = 16
    c: Symmetric(g3,g3,g0)
    c: DistanceY(g5,g1) = 16.5
    c: DistanceY(g1,g-4) = 5
FEATURE [PartDesign::Pocket] Pocket005
  BaseFeature = -> Fillet001
  Direction = (0,1,-2e-16)
  Length = 5
  Length2 = 100
  Profile = -> Sketch010
  ReferenceAxis = -> Sketch010 [N_Axis]
  Type = 1
FEATURE [PartDesign::Body] Body025  label="RightSensorBracket"
  Group = -> [ShapeBinder028,Pad025,ShapeBinder029,Pad026,Fillet001,Sketch010,Pocket005]
  Origin = -> Origin025
  Tip = -> Pocket005
FEATURE [TechDraw::DrawViewAnnotation] Annotation  label="BasePanelAnnotation"
  Font = osifont
  LineSpace = 80
  LockPosition = false
  MaxWidth = -1
  Rotation = 0
  ScaleType = 0
  Text = Base Layer
  TextSize = 5
  TextStyle = 0
  X = 109.185
  Y = 61.3858
FEATURE [TechDraw::DrawViewAnnotation] Annotation001  label="TopPanelAnnotation"
  Font = osifont
  LineSpace = 80
  LockPosition = false
  MaxWidth = -1
  Rotation = 0
  ScaleType = 0
  Text = Top Two Layers
  TextSize = 5
  TextStyle = 0
  X = 105.4
  Y = 248.209
FEATURE [TechDraw::DrawSVGTemplate] Template004
  Height = 297
  Orientation = 0
  Width = 210
FEATURE [PartDesign::ShapeBinder] ShapeBinder024
  Support = -> [Sketch007]
  TraceSupport = false
FEATURE [PartDesign::Pad] Pad022
  Direction = (0,0,-1)
  Length = 1
  Length2 = 100
  Profile = -> ShapeBinder024
  Reversed = true
  Type = 0
FEATURE [PartDesign::Body] Body022  label="UpperPlateBase"
  Group = -> [ShapeBinder024,Pad022]
  Origin = -> Origin022
  Placement = pos=(0,0,30) rot=(0,0,1;0rad)
  Tip = -> Pad022
FEATURE [TechDraw::DrawProjGroupItem] ProjItem012  label="Front007"
  CoarseView = false
  Direction = (0,0,1)
  Focus = 100
  HardHidden = false
  IsoCount = 0
  IsoHidden = false
  IsoVisible = false
  LockPosition = true
  Perspective = false
  Rotation = 0
  RotationVector = (1,0,0)
  ScaleType = 2
  SeamHidden = false
  SeamVisible = true
  SmoothHidden = false
  SmoothVisible = true
  Source = -> [Body022]
  Type = 0
  X = 0
  XDirection = (1,0,0)
  Y = 0
FEATURE [TechDraw::DrawViewDimension] Dimension043
  Arbitrary = false
  ArbitraryTolerances = false
  EqualTolerance = true
  FormatSpec = %.2f
  FormatSpecOverTolerance = %+.2f
  FormatSpecUnderTolerance = %+.2f
  Inverted = false
  LockPosition = false
  MeasureType = 1
  OverTolerance = 0
  References2D = -> [ProjItem012]
  Rotation = 0
  ScaleType = 0
  TheoreticalExact = false
  Type = 2
  UnderTolerance = 0
  X = -80.3127
  Y = -0.31972
FEATURE [TechDraw::DrawViewDimension] Dimension044
  Arbitrary = false
  ArbitraryTolerances = false
  EqualTolerance = true
  FormatSpec = %.2f
  FormatSpecOverTolerance = %+.2f
  FormatSpecUnderTolerance = %+.2f
  Inverted = false
  LockPosition = false
  MeasureType = 1
  OverTolerance = 0
  References2D = -> [ProjItem012]
  Rotation = 0
  ScaleType = 0
  TheoreticalExact = false
  Type = 1
  UnderTolerance = 0
  X = -4.31622
  Y = 39.0677
FEATURE [TechDraw::DrawViewDimension] Dimension047
  Arbitrary = false
  ArbitraryTolerances = false
  EqualTolerance = true
  FormatSpec = ⌀%.2f
  FormatSpecOverTolerance = %+.2f
  FormatSpecUnderTolerance = %+.2f
  Inverted = false
  LockPosition = false
  MeasureType = 1
  OverTolerance = 0
  References2D = -> [ProjItem012]
  Rotation = 0
  ScaleType = 0
  TheoreticalExact = false
  Type = 5
  UnderTolerance = 0
  X = -54.6613
  Y = 9.01529
FEATURE [TechDraw::DrawViewDimension] Dimension045
  Arbitrary = false
  ArbitraryTolerances = false
  EqualTolerance = true
  FormatSpec = %.2f
  FormatSpecOverTolerance = %+.2f
  FormatSpecUnderTolerance = %+.2f
  Inverted = false
  LockPosition = false
  MeasureType = 1
  OverTolerance = 0
  References2D = -> [ProjItem012]
  Rotation = 0
  ScaleType = 0
  TheoreticalExact = false
  Type = 2
  UnderTolerance = 0
  X = -47.5548
  Y = -8.77245
FEATURE [TechDraw::DrawViewDimension] Dimension046
  Arbitrary = false
  ArbitraryTolerances = false
  EqualTolerance = true
  FormatSpec = %.2f
  FormatSpecOverTolerance = %+.2f
  FormatSpecUnderTolerance = %+.2f
  Inverted = false
  LockPosition = false
  MeasureType = 1
  OverTolerance = 0
  References2D = -> [ProjItem012]
  Rotation = 0
  ScaleType = 0
  TheoreticalExact = false
  Type = 1
  UnderTolerance = 0
  X = -78.1529
  Y = -28.6902
FEATURE [TechDraw::DrawProjGroup] ProjGroup012
  Anchor = -> ProjItem012
  AutoDistribute = true
  LockPosition = false
  ProjectionType = 0
  Rotation = 0
  ScaleType = 0
  Source = -> [Body022]
  Views = -> [ProjItem012]
  X = 109.818
  Y = 62.0634
  spacingX = 15
  spacingY = 15
FEATURE [PartDesign::ShapeBinder] ShapeBinder023
  Support = -> [Sketch007]
  TraceSupport = false
FEATURE [PartDesign::Pad] Pad021
  Direction = (0,0,-1)
  Length = 2
  Length2 = 100
  Profile = -> ShapeBinder023
  Reversed = true
  Type = 0
FEATURE [PartDesign::Body] Body021  label="UpperPlateTop"
  Group = -> [ShapeBinder023,Pad021]
  Origin = -> Origin021
  Placement = pos=(0,0,31) rot=(0,0,1;0rad)
  Tip = -> Pad021
FEATURE [TechDraw::DrawProjGroupItem] ProjItem011  label="Front006"
  CoarseView = false
  Direction = (0,0,1)
  Focus = 100
  HardHidden = false
  IsoCount = 0
  IsoHidden = false
  IsoVisible = false
  LockPosition = true
  Perspective = false
  Rotation = 0
  RotationVector = (1,0,0)
  ScaleType = 2
  SeamHidden = false
  SeamVisible = true
  SmoothHidden = false
  SmoothVisible = true
  Source = -> [Body021]
  Type = 0
  X = 0
  XDirection = (1,0,0)
  Y = 0
FEATURE [TechDraw::DrawViewDimension] Dimension030
  Arbitrary = false
  ArbitraryTolerances = false
  EqualTolerance = true
  FormatSpec = %.2f
  FormatSpecOverTolerance = %+.2f
  FormatSpecUnderTolerance = %+.2f
  Inverted = false
  LockPosition = false
  MeasureType = 1
  OverTolerance = 0
  References2D = -> [ProjItem011]
  Rotation = 0
  ScaleType = 0
  TheoreticalExact = false
  Type = 1
  UnderTolerance = 0
  X = -62.1599
  Y = 12.262
FEATURE [TechDraw::DrawViewDimension] Dimension038
  Arbitrary = false
  ArbitraryTolerances = false
  EqualTolerance = true
  FormatSpec = %.2f
  FormatSpecOverTolerance = %+.2f
  FormatSpecUnderTolerance = %+.2f
  Inverted = false
  LockPosition = false
  MeasureType = 1
  OverTolerance = 0
  References2D = -> [ProjItem011]
  Rotation = 0
  ScaleType = 0
  TheoreticalExact = false
  Type = 1
  UnderTolerance = 0
  X = 43.1803
  Y = -3.73162
FEATURE [TechDraw::DrawViewDimension] Dimension039
  Arbitrary = false
  ArbitraryTolerances = false
  EqualTolerance = true
  FormatSpec = %.2f
  FormatSpecOverTolerance = %+.2f
  FormatSpecUnderTolerance = %+.2f
  Inverted = false
  LockPosition = false
  MeasureType = 1
  OverTolerance = 0
  References2D = -> [ProjItem011]
  Rotation = 0
  ScaleType = 0
  TheoreticalExact = false
  Type = 1
  UnderTolerance = 0
  X = 66.3401
  Y = 6.17971
FEATURE [TechDraw::DrawViewDimension] Dimension042
  Arbitrary = false
  ArbitraryTolerances = false
  EqualTolerance = true
  FormatSpec = ⌀%.2f
  FormatSpecOverTolerance = %+.2f
  FormatSpecUnderTolerance = %+.2f
  Inverted = false
  LockPosition = false
  MeasureType = 1
  OverTolerance = 0
  References2D = -> [ProjItem011]
  Rotation = 0
  ScaleType = 0
  TheoreticalExact = false
  Type = 5
  UnderTolerance = 0
  X = -62.3454
  Y = -7.51342
FEATURE [TechDraw::DrawViewDimension] Dimension035
  Arbitrary = false
  ArbitraryTolerances = false
  EqualTolerance = true
  FormatSpec = %.2f
  FormatSpecOverTolerance = %+.2f
  FormatSpecUnderTolerance = %+.2f
  Inverted = false
  LockPosition = false
  MeasureType = 1
  OverTolerance = 0
  References2D = -> [ProjItem011]
  Rotation = 0
  ScaleType = 0
  TheoreticalExact = false
  Type = 2
  UnderTolerance = 0
  X = 10.6534
  Y = -0.63944
FEATURE [TechDraw::DrawViewDimension] Dimension036
  Arbitrary = false
  ArbitraryTolerances = false
  EqualTolerance = true
  FormatSpec = %.2f
  FormatSpecOverTolerance = %+.2f
  FormatSpecUnderTolerance = %+.2f
  Inverted = false
  LockPosition = false
  MeasureType = 1
  OverTolerance = 0
  References2D = -> [ProjItem011]
  Rotation = 0
  ScaleType = 0
  TheoreticalExact = false
  Type = 2
  UnderTolerance = 0
  X = 4.5694
  Y = 15.245
FEATURE [TechDraw::DrawViewDimension] Dimension041
  Arbitrary = false
  ArbitraryTolerances = false
  EqualTolerance = true
  FormatSpec = %.2f
  FormatSpecOverTolerance = %+.2f
  FormatSpecUnderTolerance = %+.2f
  Inverted = false
  LockPosition = false
  MeasureType = 1
  OverTolerance = 0
  References2D = -> [ProjItem011]
  Rotation = 0
  ScaleType = 0
  TheoreticalExact = false
  Type = 2
  UnderTolerance = 0
  X = -58.1056
  Y = -31.4726
FEATURE [TechDraw::DrawViewDimension] Dimension028
  Arbitrary = false
  ArbitraryTolerances = false
  EqualTolerance = true
  FormatSpec = %.2f
  FormatSpecOverTolerance = %+.2f
  FormatSpecUnderTolerance = %+.2f
  Inverted = false
  LockPosition = false
  MeasureType = 1
  OverTolerance = 0
  References2D = -> [ProjItem011]
  Rotation = 0
  ScaleType = 0
  TheoreticalExact = false
  Type = 2
  UnderTolerance = 0
  X = -83.3827
  Y = 0.350236
FEATURE [TechDraw::DrawViewDimension] Dimension031
  Arbitrary = false
  ArbitraryTolerances = false
  EqualTolerance = true
  FormatSpec = %.2f
  FormatSpecOverTolerance = %+.2f
  FormatSpecUnderTolerance = %+.2f
  Inverted = false
  LockPosition = false
  MeasureType = 1
  OverTolerance = 0
  References2D = -> [ProjItem011]
  Rotation = 0
  ScaleType = 0
  TheoreticalExact = false
  Type = 1
  UnderTolerance = 0
  X = -44.1972
  Y = 11.9422
FEATURE [TechDraw::DrawViewDimension] Dimension033
  Arbitrary = false
  ArbitraryTolerances = false
  EqualTolerance = true
  FormatSpec = %.2f
  FormatSpecOverTolerance = %+.2f
  FormatSpecUnderTolerance = %+.2f
  Inverted = false
  LockPosition = false
  MeasureType = 1
  OverTolerance = 0
  References2D = -> [ProjItem011]
  Rotation = 0
  ScaleType = 0
  TheoreticalExact = false
  Type = 2
  UnderTolerance = 0
  X = -21.2077
  Y = -0.31972
FEATURE [TechDraw::DrawViewDimension] Dimension040
  Arbitrary = false
  ArbitraryTolerances = false
  EqualTolerance = true
  FormatSpec = %.2f
  FormatSpecOverTolerance = %+.2f
  FormatSpecUnderTolerance = %+.2f
  Inverted = false
  LockPosition = false
  MeasureType = 1
  OverTolerance = 0
  References2D = -> [ProjItem011]
  Rotation = 0
  ScaleType = 0
  TheoreticalExact = false
  Type = 1
  UnderTolerance = 0
  X = -83.4282
  Y = -30.9282
FEATURE [TechDraw::DrawProjGroup] ProjGroup011
  Anchor = -> ProjItem011
  AutoDistribute = true
  LockPosition = false
  ProjectionType = 0
  Rotation = 0
  ScaleType = 0
  Source = -> [Body021]
  Views = -> [ProjItem011]
  X = 108.544
  Y = 138.845
  spacingX = 15
  spacingY = 15
FEATURE [PartDesign::ShapeBinder] ShapeBinder030  label="SensorBracketHoleBinder"
  Support = -> [Sketch008]
  TraceSupport = false
FEATURE [PartDesign::Pocket] Pocket006
  BaseFeature = -> Pocket003
  Direction = (0,0,-1)
  Length = 5
  Length2 = 100
  Profile = -> ShapeBinder030
  Type = 1
FEATURE [TechDraw::DrawSVGTemplate] Template005
  Height = 297
  Orientation = 0
  Width = 210
FEATURE [Sketcher::SketchObject] Sketch011  label="BracketFrontSketch"
  ExternalGeometry = -> [Sketch008]
  FullyConstrained = true
  MapMode = 5
  Placement = pos=(0,0,0) rot=(1,0,0;1.5708rad)
  Support = -> [XZ_Plane]
  sketch-geometry (21):
    g0: LineSegment StartX=-21 StartY=2.13e-14 StartZ=0 EndX=-45 EndY=2.22e-14 EndZ=0
    g1: LineSegment StartX=-45 StartY=2.22e-14 StartZ=0 EndX=-45 EndY=30 EndZ=0
    g2: LineSegment StartX=-45 StartY=30 StartZ=0 EndX=-21 EndY=30 EndZ=0
    g3: LineSegment StartX=-21 StartY=30 StartZ=0 EndX=-21 EndY=2.13e-14 EndZ=0
    g4: Circle CenterX=-40 CenterY=25 CenterZ=0 NormalX=0 NormalY=0 NormalZ=1 AngleXU=0 Radius=1
    g5: Circle CenterX=-26 CenterY=25 CenterZ=0 NormalX=0 NormalY=0 NormalZ=1 AngleXU=0 Radius=1
    g6: LineSegment StartX=-41 StartY=11.5 StartZ=0 EndX=-25 EndY=11.5 EndZ=0
    g7: LineSegment StartX=-25 StartY=11.5 StartZ=0 EndX=-25 EndY=8.5 EndZ=0
    g8: LineSegment StartX=-25 StartY=8.5 StartZ=0 EndX=-41 EndY=8.5 EndZ=0
    g9: LineSegment StartX=-41 StartY=8.5 StartZ=0 EndX=-41 EndY=11.5 EndZ=0
    g10: LineSegment StartX=21 StartY=0 StartZ=0 EndX=45 EndY=0 EndZ=0
    g11: LineSegment StartX=45 StartY=0 StartZ=0 EndX=45 EndY=30 EndZ=0
    g12: LineSegment StartX=45 StartY=30 StartZ=0 EndX=21 EndY=30 EndZ=0
    g13: LineSegment StartX=21 StartY=30 StartZ=0 EndX=21 EndY=0 EndZ=0
    g14: LineSegment StartX=41 StartY=11.5 StartZ=0 EndX=25 EndY=11.5 EndZ=0
    g15: LineSegment StartX=25 StartY=11.5 StartZ=0 EndX=25 EndY=8.5 EndZ=0
    g16: LineSegment StartX=25 StartY=8.5 StartZ=0 EndX=41 EndY=8.5 EndZ=0
    g17: LineSegment StartX=41 StartY=8.5 StartZ=0 EndX=41 EndY=11.5 EndZ=0
    g18: Circle CenterX=26 CenterY=25 CenterZ=0 NormalX=0 NormalY=0 NormalZ=1 AngleXU=0 Radius=1
    g19: Circle CenterX=40 CenterY=25 CenterZ=0 NormalX=0 NormalY=0 NormalZ=1 AngleXU=0 Radius=1
    g20: LineSegment StartX=-33 StartY=30 StartZ=0 EndX=-33 EndY=2.13e-14 EndZ=0
  constraints (52):
    c: Coincident(g0,g1)
    c: Coincident(g1,g2)
    c: Coincident(g2,g3)
    c: Coincident(g3,g0)
    c: Horizontal(g2)
    c: Vertical(g1)
    c: Vertical(g3)
    c: Coincident(g0,g-3)
    c: Coincident(g-3,g0)
    c: DistanceY(g1,g1) = 30
    c: Coincident(g6,g7)
    c: Coincident(g7,g8)
    c: Coincident(g8,g9)
    c: Coincident(g9,g6)
    c: Horizontal(g8)
    c: Vertical(g7)
    c: Vertical(g9)
    c: Coincident(g10,g11)
    c: Coincident(g11,g12)
    c: Coincident(g12,g13)
    c: Coincident(g13,g10)
    c: Horizontal(g12)
    c: Vertical(g11)
    c: Coincident(g10,g-4)
    c: Coincident(g14,g15)
    c: Coincident(g15,g16)
    c: Coincident(g16,g17)
    c: Coincident(g17,g14)
    c: Horizontal(g14)
    c: Horizontal(g16)
    c: Vertical(g15)
    c: Vertical(g17)
    c: Coincident(g10,g-4)
    c: Symmetric(g2,g12,g-2)
    c: PointOnObject(g20,g2)
    c: PointOnObject(g20,g0)
    c: Symmetric(g2,g1,g20)
    c: Symmetric(g5,g4,g20)
    c: Symmetric(g5,g18,g-2)
    c: Symmetric(g4,g19,g-2)
    c: Symmetric(g6,g6,g20)
    c: Symmetric(g6,g14,g-2)
    c: Symmetric(g16,g8,g-2)
    c: Equal(g4,g5)
    c: Equal(g5,g18)
    c: Equal(g18,g19)
    c: Diameter(g4) = 2
    c: DistanceY(g4,g1) = 5
    c: DistanceX(g4,g5) = 14
    c: DistanceX(g6,g6) = 16
    c: DistanceY(g7,g7) = 3
    c: DistanceY(g6,g5) = 13.5
FEATURE [PartDesign::Body] Body  label="ChassisPlate"
  Group = -> [Sketch,Sketch001,Pad,ShapeBinder,Pocket,Sketch002,Sketch003,Sketch004,Sketch005,ShapeBinder016,Pocket001,Sketch006,Sketch007,ShapeBinder025,Pocket003,Sketch008,ShapeBinder030,Pocket006,Sketch011]
  Origin = -> Origin
  Tip = -> Pocket006
FEATURE [TechDraw::DrawProjGroupItem] ProjItem006  label="Front001"
  CoarseView = false
  Direction = (0,0,-1)
  Focus = 100
  HardHidden = false
  IsoCount = 0
  IsoHidden = false
  IsoVisible = false
  LockPosition = true
  Perspective = false
  Rotation = 0
  RotationVector = (1,0,0)
  ScaleType = 2
  SeamHidden = false
  SeamVisible = true
  SmoothHidden = false
  SmoothVisible = true
  Source = -> [Body]
  Type = 0
  X = 0
  XDirection = (1,0,0)
  Y = 0
FEATURE [TechDraw::DrawProjGroup] ProjGroup006  label="ProjGroup001"
  Anchor = -> ProjItem006
  AutoDistribute = true
  LockPosition = false
  ProjectionType = 0
  Rotation = 0
  ScaleType = 0
  Source = -> [Body]
  Views = -> [ProjItem006]
  X = 127.793
  Y = 183.726
  spacingX = 15
  spacingY = 15
FEATURE [TechDraw::DrawProjGroupItem] ProjItem  label="Front"
  CoarseView = false
  Direction = (0,0,1)
  Focus = 100
  HardHidden = false
  IsoCount = 0
  IsoHidden = false
  IsoVisible = false
  LockPosition = true
  Perspective = false
  Rotation = 0
  RotationVector = (-1,0,0)
  ScaleType = 2
  SeamHidden = false
  SeamVisible = true
  SmoothHidden = false
  SmoothVisible = true
  Source = -> [Body,Body019,Body018,Body017,Body020]
  Type = 0
  X = 0
  XDirection = (-1,0,0)
  Y = 0
FEATURE [TechDraw::DrawProjGroup] ProjGroup
  Anchor = -> ProjItem
  AutoDistribute = true
  LockPosition = false
  ProjectionType = 0
  Rotation = 0
  ScaleType = 0
  Source = -> [Body,Body019,Body018,Body017,Body020]
  Views = -> [ProjItem]
  X = 111.096
  Y = 157.442
  spacingX = 15
  spacingY = 15
FEATURE [TechDraw::DrawViewDimension] Dimension071
  Arbitrary = false
  ArbitraryTolerances = false
  EqualTolerance = true
  FormatSpec = %.2f
  FormatSpecOverTolerance = %+.2f
  FormatSpecUnderTolerance = %+.2f
  Inverted = false
  LockPosition = false
  MeasureType = 1
  OverTolerance = 0
  References2D = -> [ProjItem006]
  Rotation = 0
  ScaleType = 0
  TheoreticalExact = false
  Type = 2
  UnderTolerance = 0
  X = 43.513
  Y = -88.4568
FEATURE [TechDraw::DrawViewDimension] Dimension073
  Arbitrary = false
  ArbitraryTolerances = false
  EqualTolerance = true
  FormatSpec = ⌀%.2f
  FormatSpecOverTolerance = %+.2f
  FormatSpecUnderTolerance = %+.2f
  Inverted = false
  LockPosition = false
  MeasureType = 1
  OverTolerance = 0
  References2D = -> [ProjItem006]
  Rotation = 0
  ScaleType = 0
  TheoreticalExact = false
  Type = 5
  UnderTolerance = 0
  X = 53.3999
  Y = 42.2467
FEATURE [TechDraw::DrawViewDimension] Dimension074
  Arbitrary = false
  ArbitraryTolerances = false
  EqualTolerance = true
  FormatSpec = ⌀%.2f
  FormatSpecOverTolerance = %+.2f
  FormatSpecUnderTolerance = %+.2f
  Inverted = false
  LockPosition = false
  MeasureType = 1
  OverTolerance = 0
  References2D = -> [ProjItem006]
  Rotation = 0
  ScaleType = 0
  TheoreticalExact = false
  Type = 5
  UnderTolerance = 0
  X = 27.7072
  Y = -57.7725
FEATURE [TechDraw::DrawViewDimension] Dimension075
  Arbitrary = false
  ArbitraryTolerances = false
  EqualTolerance = true
  FormatSpec = ⌀%.2f
  FormatSpecOverTolerance = %+.2f
  FormatSpecUnderTolerance = %+.2f
  Inverted = false
  LockPosition = false
  MeasureType = 1
  OverTolerance = 0
  References2D = -> [ProjItem006]
  Rotation = 0
  ScaleType = 0
  TheoreticalExact = false
  Type = 5
  UnderTolerance = 0
  X = -13.519
  Y = -54.7518
FEATURE [TechDraw::DrawViewDimension] Dimension076
  Arbitrary = false
  ArbitraryTolerances = false
  EqualTolerance = true
  FormatSpec = ⌀%.2f
  FormatSpecOverTolerance = %+.2f
  FormatSpecUnderTolerance = %+.2f
  Inverted = false
  LockPosition = false
  MeasureType = 1
  OverTolerance = 0
  References2D = -> [ProjItem006]
  Rotation = 0
  ScaleType = 0
  TheoreticalExact = false
  Type = 5
  UnderTolerance = 0
  X = 55.0897
  Y = 74.5232
FEATURE [TechDraw::DrawViewDimension] Dimension083
  Arbitrary = false
  ArbitraryTolerances = false
  EqualTolerance = true
  FormatSpec = %.2f
  FormatSpecOverTolerance = %+.2f
  FormatSpecUnderTolerance = %+.2f
  Inverted = false
  LockPosition = false
  MeasureType = 1
  OverTolerance = 0
  References2D = -> [ProjItem006]
  Rotation = 0
  ScaleType = 0
  TheoreticalExact = false
  Type = 1
  UnderTolerance = 0
  X = 68.6811
  Y = -74.0947
FEATURE [TechDraw::DrawViewDimension] Dimension084
  Arbitrary = false
  ArbitraryTolerances = false
  EqualTolerance = true
  FormatSpec = %.2f
  FormatSpecOverTolerance = %+.2f
  FormatSpecUnderTolerance = %+.2f
  Inverted = false
  LockPosition = false
  MeasureType = 1
  OverTolerance = 0
  References2D = -> [ProjItem]
  Rotation = 0
  ScaleType = 0
  TheoreticalExact = false
  Type = 1
  UnderTolerance = 0
  X = 0
  Y = -38
FEATURE [TechDraw::DrawViewDimension] Dimension085
  Arbitrary = false
  ArbitraryTolerances = false
  EqualTolerance = true
  FormatSpec = %.2f
  FormatSpecOverTolerance = %+.2f
  FormatSpecUnderTolerance = %+.2f
  Inverted = false
  LockPosition = false
  MeasureType = 1
  OverTolerance = 0
  References2D = -> [ProjItem]
  Rotation = 0
  ScaleType = 0
  TheoreticalExact = false
  Type = 2
  UnderTolerance = 0
  X = -47.6414
  Y = 8.10677
FEATURE [TechDraw::DrawViewDimension] Dimension086
  Arbitrary = false
  ArbitraryTolerances = false
  EqualTolerance = true
  FormatSpec = %.2f
  FormatSpecOverTolerance = %+.2f
  FormatSpecUnderTolerance = %+.2f
  Inverted = false
  LockPosition = false
  MeasureType = 1
  OverTolerance = 0
  References2D = -> [ProjItem]
  Rotation = 0
  ScaleType = 0
  TheoreticalExact = false
  Type = 2
  UnderTolerance = 0
  X = -57.2436
  Y = 75.5436
FEATURE [TechDraw::DrawViewDimension] Dimension087
  Arbitrary = false
  ArbitraryTolerances = false
  EqualTolerance = true
  FormatSpec = %.2f
  FormatSpecOverTolerance = %+.2f
  FormatSpecUnderTolerance = %+.2f
  Inverted = false
  LockPosition = false
  MeasureType = 1
  OverTolerance = 0
  References2D = -> [ProjItem]
  Rotation = 0
  ScaleType = 0
  TheoreticalExact = false
  Type = 1
  UnderTolerance = 0
  X = -54
  Y = 56
FEATURE [TechDraw::DrawPage] Page  label="BreadboardRodGluingGuide"
  KeepUpdated = true
  NextBalloonIndex = 1
  ProjectionType = 0
  Template = -> Template
  Views = -> [ProjGroup,Dimension084,Dimension085,Dimension086,Dimension087]
FEATURE [TechDraw::DrawViewDimension] Dimension110
  Arbitrary = false
  ArbitraryTolerances = false
  EqualTolerance = true
  FormatSpec = %.2f
  FormatSpecOverTolerance = %+.2f
  FormatSpecUnderTolerance = %+.2f
  Inverted = false
  LockPosition = false
  MeasureType = 1
  OverTolerance = 0
  References2D = -> [ProjItem006]
  Rotation = 0
  ScaleType = 0
  TheoreticalExact = false
  Type = 2
  UnderTolerance = 0
  X = 44.3991
  Y = 85.7305
FEATURE [TechDraw::DrawViewDimension] Dimension119
  Arbitrary = false
  ArbitraryTolerances = false
  EqualTolerance = true
  FormatSpec = %.2f
  FormatSpecOverTolerance = %+.2f
  FormatSpecUnderTolerance = %+.2f
  Inverted = false
  LockPosition = false
  MeasureType = 1
  OverTolerance = 0
  References2D = -> [ProjItem006]
  Rotation = 0
  ScaleType = 0
  TheoreticalExact = false
  Type = 1
  UnderTolerance = 0
  X = -57.5
  Y = 73.1539
FEATURE [TechDraw::DrawViewDimension] Dimension120
  Arbitrary = false
  ArbitraryTolerances = false
  EqualTolerance = true
  FormatSpec = %.2f
  FormatSpecOverTolerance = %+.2f
  FormatSpecUnderTolerance = %+.2f
  Inverted = false
  LockPosition = false
  MeasureType = 1
  OverTolerance = 0
  References2D = -> [ProjItem006]
  Rotation = 0
  ScaleType = 0
  TheoreticalExact = false
  Type = 1
  UnderTolerance = 0
  X = -32.1385
  Y = 73.3693
FEATURE [PartDesign::ShapeBinder] ShapeBinder031
  Support = -> [Sketch011]
  TraceSupport = false
FEATURE [PartDesign::Pocket] Pocket007
  BaseFeature = -> Fillet
  Direction = (0,-1,-2e-16)
  Length = 5
  Length2 = 100
  Profile = -> ShapeBinder031
  Type = 1
FEATURE [PartDesign::Body] Body023  label="LeftSensorBracket"
  Group = -> [ShapeBinder026,Pad023,ShapeBinder027,Pad024,Fillet,ShapeBinder031,Pocket007]
  Origin = -> Origin023
  Tip = -> Pocket007
FEATURE [TechDraw::DrawProjGroupItem] ProjItem013  label="Front008"
  CoarseView = false
  Direction = (0,-1,0)
  Focus = 100
  HardHidden = false
  IsoCount = 0
  IsoHidden = false
  IsoVisible = false
  LockPosition = true
  Perspective = false
  Rotation = 0
  RotationVector = (1,0,0)
  Scale = 1.5
  ScaleType = 2
  SeamHidden = false
  SeamVisible = true
  SmoothHidden = false
  SmoothVisible = true
  Source = -> [Body023]
  Type = 0
  X = 0
  XDirection = (1,0,0)
  Y = 0
FEATURE [TechDraw::DrawProjGroupItem] ProjItem014  label="Right"
  CoarseView = false
  Direction = (1,-1e-16,0)
  Focus = 100
  HardHidden = false
  IsoCount = 0
  IsoHidden = false
  IsoVisible = false
  LockPosition = false
  Perspective = false
  Rotation = 0
  RotationVector = (1,0,0)
  Scale = 1.5
  ScaleType = 2
  SeamHidden = false
  SeamVisible = true
  SmoothHidden = false
  SmoothVisible = true
  Source = -> [Body023]
  Type = 2
  X = -66.1378
  XDirection = (1e-16,1,0)
  Y = 0
FEATURE [TechDraw::DrawProjGroupItem] ProjItem015  label="Top"
  CoarseView = false
  Direction = (0,0,1)
  Focus = 100
  HardHidden = false
  IsoCount = 0
  IsoHidden = false
  IsoVisible = false
  LockPosition = false
  Perspective = false
  Rotation = 0
  RotationVector = (1,0,0)
  Scale = 1.5
  ScaleType = 2
  SeamHidden = false
  SeamVisible = true
  SmoothHidden = false
  SmoothVisible = true
  Source = -> [Body023]
  Type = 4
  X = 0
  XDirection = (1,0,0)
  Y = -78.4135
FEATURE [TechDraw::DrawProjGroupItem] ProjItem016  label="FrontTopRight"
  CoarseView = false
  Direction = (0.57735,-0.57735,0.57735)
  Focus = 100
  HardHidden = false
  IsoCount = 0
  IsoHidden = false
  IsoVisible = false
  LockPosition = false
  Perspective = false
  Rotation = 0
  RotationVector = (1,0,0)
  Scale = 1.5
  ScaleType = 2
  SeamHidden = false
  SeamVisible = true
  SmoothHidden = false
  SmoothVisible = true
  Source = -> [Body023]
  Type = 7
  X = -72.2756
  XDirection = (0.707107,0.707107,0)
  Y = -74.8154
FEATURE [TechDraw::DrawProjGroup] ProjGroup013
  Anchor = -> ProjItem013
  AutoDistribute = true
  LockPosition = false
  ProjectionType = 0
  Rotation = 0
  Scale = 1.5
  ScaleType = 1
  Source = -> [Body023]
  Views = -> [ProjItem013,ProjItem014,ProjItem015,ProjItem016]
  X = 111.839
  Y = 204.206
  spacingX = 15
  spacingY = 15
FEATURE [TechDraw::DrawViewDimension] Dimension090
  Arbitrary = false
  ArbitraryTolerances = false
  EqualTolerance = true
  FormatSpec = %.2f
  FormatSpecOverTolerance = %+.2f
  FormatSpecUnderTolerance = %+.2f
  Inverted = false
  LockPosition = false
  MeasureType = 1
  OverTolerance = 0
  References2D = -> [ProjItem013]
  Rotation = 0
  ScaleType = 0
  TheoreticalExact = false
  Type = 1
  UnderTolerance = 0
  X = 1.78705
  Y = -31.2361
FEATURE [TechDraw::DrawViewDimension] Dimension091
  Arbitrary = false
  ArbitraryTolerances = false
  EqualTolerance = true
  FormatSpec = %.2f
  FormatSpecOverTolerance = %+.2f
  FormatSpecUnderTolerance = %+.2f
  Inverted = false
  LockPosition = false
  MeasureType = 1
  OverTolerance = 0
  References2D = -> [ProjItem013]
  Rotation = 0
  ScaleType = 0
  TheoreticalExact = false
  Type = 1
  UnderTolerance = 0
  X = -0.979858
  Y = -12.5987
FEATURE [TechDraw::DrawViewDimension] Dimension104
  Arbitrary = false
  ArbitraryTolerances = false
  EqualTolerance = true
  FormatSpec = %.2f
  FormatSpecOverTolerance = %+.2f
  FormatSpecUnderTolerance = %+.2f
  Inverted = false
  LockPosition = false
  MeasureType = 1
  OverTolerance = 0
  References2D = -> [ProjItem013]
  Rotation = 0
  ScaleType = 0
  TheoreticalExact = false
  Type = 2
  UnderTolerance = 0
  X = -39.5791
  Y = 4.99058
FEATURE [TechDraw::DrawViewDimension] Dimension105
  Arbitrary = false
  ArbitraryTolerances = false
  EqualTolerance = true
  FormatSpec = %.2f
  FormatSpecOverTolerance = %+.2f
  FormatSpecUnderTolerance = %+.2f
  Inverted = false
  LockPosition = false
  MeasureType = 1
  OverTolerance = 0
  References2D = -> [ProjItem015]
  Rotation = 0
  ScaleType = 0
  TheoreticalExact = false
  Type = 2
  UnderTolerance = 0
  X = -34.4616
  Y = 0.293957
FEATURE [TechDraw::DrawViewDimension] Dimension107
  Arbitrary = false
  ArbitraryTolerances = false
  EqualTolerance = true
  FormatSpec = ⌀%.2f
  FormatSpecOverTolerance = %+.2f
  FormatSpecUnderTolerance = %+.2f
  Inverted = false
  LockPosition = false
  MeasureType = 1
  OverTolerance = 0
  References2D = -> [ProjItem013]
  Rotation = 0
  ScaleType = 0
  TheoreticalExact = false
  Type = 5
  UnderTolerance = 0
  X = 6.28415
  Y = 31.0221
FEATURE [TechDraw::DrawViewDimension] Dimension108
  Arbitrary = false
  ArbitraryTolerances = false
  EqualTolerance = true
  FormatSpec = ⌀%.2f
  FormatSpecOverTolerance = %+.2f
  FormatSpecUnderTolerance = %+.2f
  Inverted = false
  LockPosition = false
  MeasureType = 1
  OverTolerance = 0
  References2D = -> [ProjItem015]
  Rotation = 0
  ScaleType = 0
  TheoreticalExact = false
  Type = 5
  UnderTolerance = 0
  X = 2.14676
  Y = 14.759
FEATURE [TechDraw::DrawViewDimension] Dimension111
  Arbitrary = false
  ArbitraryTolerances = false
  EqualTolerance = true
  FormatSpec = %.2f
  FormatSpecOverTolerance = %+.2f
  FormatSpecUnderTolerance = %+.2f
  Inverted = false
  LockPosition = false
  MeasureType = 1
  OverTolerance = 0
  References2D = -> [ProjItem013]
  Rotation = 0
  ScaleType = 0
  TheoreticalExact = false
  Type = 2
  UnderTolerance = 0
  X = 21.1092
  Y = 11.6165
FEATURE [TechDraw::DrawViewDimension] Dimension112
  Arbitrary = false
  ArbitraryTolerances = false
  EqualTolerance = true
  FormatSpec = %.2f
  FormatSpecOverTolerance = %+.2f
  FormatSpecUnderTolerance = %+.2f
  Inverted = false
  LockPosition = false
  MeasureType = 1
  OverTolerance = 0
  References2D = -> [ProjItem015]
  Rotation = 0
  ScaleType = 0
  TheoreticalExact = false
  Type = 2
  UnderTolerance = 0
  X = -24.7904
  Y = 11.2784
FEATURE [TechDraw::DrawViewDimension] Dimension113
  Arbitrary = false
  ArbitraryTolerances = false
  EqualTolerance = true
  FormatSpec = %.2f
  FormatSpecOverTolerance = %+.2f
  FormatSpecUnderTolerance = %+.2f
  Inverted = false
  LockPosition = false
  MeasureType = 1
  OverTolerance = 0
  References2D = -> [ProjItem015]
  Rotation = 0
  ScaleType = 0
  TheoreticalExact = false
  Type = 1
  UnderTolerance = 0
  X = -24.0211
  Y = 1.98175
FEATURE [TechDraw::DrawViewDimension] Dimension114
  Arbitrary = false
  ArbitraryTolerances = false
  EqualTolerance = true
  FormatSpec = %.2f
  FormatSpecOverTolerance = %+.2f
  FormatSpecUnderTolerance = %+.2f
  Inverted = false
  LockPosition = false
  MeasureType = 1
  OverTolerance = 0
  References2D = -> [ProjItem015]
  Rotation = 0
  ScaleType = 0
  TheoreticalExact = false
  Type = 1
  UnderTolerance = 0
  X = -2.00886
  Y = 4.33884
FEATURE [TechDraw::DrawViewDimension] Dimension115
  Arbitrary = false
  ArbitraryTolerances = false
  EqualTolerance = true
  FormatSpec = %.2f
  FormatSpecOverTolerance = %+.2f
  FormatSpecUnderTolerance = %+.2f
  Inverted = false
  LockPosition = false
  MeasureType = 1
  OverTolerance = 0
  References2D = -> [ProjItem013]
  Rotation = 0
  ScaleType = 0
  TheoreticalExact = false
  Type = 1
  UnderTolerance = 0
  X = -13.5978
  Y = 8.25071
FEATURE [TechDraw::DrawViewDimension] Dimension116
  Arbitrary = false
  ArbitraryTolerances = false
  EqualTolerance = true
  FormatSpec = %.2f
  FormatSpecOverTolerance = %+.2f
  FormatSpecUnderTolerance = %+.2f
  Inverted = false
  LockPosition = false
  MeasureType = 1
  OverTolerance = 0
  References2D = -> [ProjItem013]
  Rotation = 0
  ScaleType = 0
  TheoreticalExact = false
  Type = 1
  UnderTolerance = 0
  X = 0
  Y = 15.9843
FEATURE [TechDraw::DrawViewDimension] Dimension117
  Arbitrary = false
  ArbitraryTolerances = false
  EqualTolerance = true
  FormatSpec = %.2f
  FormatSpecOverTolerance = %+.2f
  FormatSpecUnderTolerance = %+.2f
  Inverted = false
  LockPosition = false
  MeasureType = 1
  OverTolerance = 0
  References2D = -> [ProjItem013]
  Rotation = 0
  ScaleType = 0
  TheoreticalExact = false
  Type = 2
  UnderTolerance = 0
  X = 23.5925
  Y = -14.2623
FEATURE [TechDraw::DrawViewDimension] Dimension118
  Arbitrary = false
  ArbitraryTolerances = false
  EqualTolerance = true
  FormatSpec = %.2f
  FormatSpecOverTolerance = %+.2f
  FormatSpecUnderTolerance = %+.2f
  Inverted = false
  LockPosition = false
  MeasureType = 1
  OverTolerance = 0
  References2D = -> [ProjItem013]
  Rotation = 0
  ScaleType = 0
  TheoreticalExact = false
  Type = 2
  UnderTolerance = 0
  X = 31.9941
  Y = 4.9541
FEATURE [TechDraw::DrawViewDimension] Dimension
  Arbitrary = false
  ArbitraryTolerances = false
  EqualTolerance = true
  FormatSpec = %.2f
  FormatSpecOverTolerance = %+.2f
  FormatSpecUnderTolerance = %+.2f
  Inverted = false
  LockPosition = false
  MeasureType = 1
  OverTolerance = 0
  References2D = -> [ProjItem006]
  Rotation = 0
  ScaleType = 0
  TheoreticalExact = false
  Type = 2
  UnderTolerance = 0
  X = 48.9583
  Y = -69.4669
FEATURE [TechDraw::DrawViewDimension] Dimension121
  Arbitrary = false
  ArbitraryTolerances = false
  EqualTolerance = true
  FormatSpec = %.2f
  FormatSpecOverTolerance = %+.2f
  FormatSpecUnderTolerance = %+.2f
  Inverted = false
  LockPosition = false
  MeasureType = 1
  OverTolerance = 0
  References2D = -> [ProjItem006]
  Rotation = 0
  ScaleType = 0
  TheoreticalExact = false
  Type = 2
  UnderTolerance = 0
  X = 58.0515
  Y = -66.9681
FEATURE [TechDraw::DrawViewDimension] Dimension122
  Arbitrary = false
  ArbitraryTolerances = false
  EqualTolerance = true
  FormatSpec = ⌀%.2f
  FormatSpecOverTolerance = %+.2f
  FormatSpecUnderTolerance = %+.2f
  Inverted = false
  LockPosition = false
  MeasureType = 1
  OverTolerance = 0
  References2D = -> [ProjItem006]
  Rotation = 0
  ScaleType = 0
  TheoreticalExact = false
  Type = 5
  UnderTolerance = 0
  X = 49.7683
  Y = -37.6906
FEATURE [TechDraw::DrawPage] Page003  label="CuttingLayout"
  KeepUpdated = true
  NextBalloonIndex = 1
  ProjectionType = 0
  Template = -> Template003
  Views = -> [ProjGroup006,ProjGroup007,ProjGroup008,ProjGroup009,Dimension017,Dimension018,Dimension019,Dimension020,Dimension,Dimension071,Dimension073,Dimension074,Dimension075,Dimension076,Dimension083,Dimension110,Dimension119,Dimension120,Dimension121,Dimension122]
FEATURE [TechDraw::DrawProjGroupItem] ProjItem017  label="Front009"
  CoarseView = false
  Direction = (0,0,1)
  Focus = 100
  HardHidden = false
  IsoCount = 0
  IsoHidden = false
  IsoVisible = false
  LockPosition = true
  Perspective = false
  Rotation = 0
  RotationVector = (1,0,0)
  ScaleType = 2
  SeamHidden = false
  SeamVisible = true
  SmoothHidden = false
  SmoothVisible = true
  Source = -> [Body021]
  Type = 0
  X = 0
  XDirection = (1,0,0)
  Y = 0
FEATURE [TechDraw::DrawProjGroup] ProjGroup014
  Anchor = -> ProjItem017
  AutoDistribute = true
  LockPosition = false
  ProjectionType = 0
  Rotation = 0
  ScaleType = 0
  Source = -> [Body021]
  Views = -> [ProjItem017]
  X = 107.919
  Y = 215.033
  spacingX = 15
  spacingY = 15
FEATURE [TechDraw::DrawViewDimension] Dimension029
  Arbitrary = false
  ArbitraryTolerances = false
  EqualTolerance = true
  FormatSpec = %.2f
  FormatSpecOverTolerance = %+.2f
  FormatSpecUnderTolerance = %+.2f
  Inverted = false
  LockPosition = false
  MeasureType = 1
  OverTolerance = 0
  References2D = -> [ProjItem011]
  Rotation = 0
  ScaleType = 0
  TheoreticalExact = false
  Type = 1
  UnderTolerance = 0
  X = 0
  Y = 36.5578
FEATURE [TechDraw::DrawViewDimension] Dimension032
  Arbitrary = false
  ArbitraryTolerances = false
  EqualTolerance = true
  FormatSpec = %.2f
  FormatSpecOverTolerance = %+.2f
  FormatSpecUnderTolerance = %+.2f
  Inverted = false
  LockPosition = false
  MeasureType = 1
  OverTolerance = 0
  References2D = -> [ProjItem011]
  Rotation = 0
  ScaleType = 0
  TheoreticalExact = false
  Type = 2
  UnderTolerance = 0
  X = -12.7351
  Y = 21.1887
FEATURE [TechDraw::DrawPage] Page004  label="UpperPlateDrawing"
  KeepUpdated = true
  NextBalloonIndex = 1
  ProjectionType = 0
  Template = -> Template004
  Views = -> [ProjGroup011,ProjGroup012,Dimension028,Dimension029,Dimension030,Dimension031,Dimension032,Dimension033,Dimension035,Dimension036,Dimension038,Dimension039,Dimension040,Dimension041,Dimension042,Dimension043,Dimension044,Dimension045,Dimension046,Dimension047,Annotation,Annotation001,ProjGroup014]
FEATURE [TechDraw::DrawViewDimension] Dimension123
  Arbitrary = false
  ArbitraryTolerances = false
  EqualTolerance = true
  FormatSpec = %.2f
  FormatSpecOverTolerance = %+.2f
  FormatSpecUnderTolerance = %+.2f
  Inverted = false
  LockPosition = false
  MeasureType = 1
  OverTolerance = 0
  References2D = -> [ProjItem014]
  Rotation = 0
  ScaleType = 0
  TheoreticalExact = false
  Type = 1
  UnderTolerance = 0
  X = 0
  Y = -30.7318
FEATURE [TechDraw::DrawHatch] Hatch  label="HatchF2"
  HatchPattern = /Applications/FreeCAD 0.20 27078.app/Contents/Resources/share/Mod/TechDraw/Patterns/simple.svg
  Source = -> ProjItem013 [Face2]
FEATURE [TechDraw::DrawViewDimension] Dimension124
  Arbitrary = false
  ArbitraryTolerances = false
  EqualTolerance = true
  FormatSpec = %.2f
  FormatSpecOverTolerance = %+.2f
  FormatSpecUnderTolerance = %+.2f
  Inverted = false
  LockPosition = false
  MeasureType = 1
  OverTolerance = 0
  References2D = -> [ProjItem013]
  Rotation = 0
  ScaleType = 0
  TheoreticalExact = false
  Type = 1
  UnderTolerance = 0
  X = -25.4555
  Y = -6.37425
FEATURE [TechDraw::DrawPage] Page005  label="BracketDrawing"
  KeepUpdated = true
  NextBalloonIndex = 1
  ProjectionType = 0
  Template = -> Template005
  Views = -> [ProjGroup013,Dimension090,Dimension091,Dimension104,Dimension105,Dimension107,Dimension108,Dimension111,Dimension112,Dimension113,Dimension114,Dimension115,Dimension116,Dimension117,Dimension118,Dimension123,Dimension124]
FEATURE [App::DocumentObjectGroup] Group  label="Drawings"
  Group = -> [Page004,Page,Page005,Page003]
FEATURE [TechDraw::DrawSVGTemplate] Template006
  Height = 297
  Orientation = 0
  Width = 210
FEATURE [TechDraw::DrawProjGroupItem] ProjItem018  label="Front010"
  CoarseView = false
  Direction = (0,0,1)
  Focus = 100
  HardHidden = false
  IsoCount = 0
  IsoHidden = false
  IsoVisible = false
  LockPosition = true
  Perspective = false
  Rotation = 0
  RotationVector = (1,0,0)
  ScaleType = 2
  SeamHidden = false
  SeamVisible = true
  SmoothHidden = false
  SmoothVisible = true
  Source = -> [Body,Body021,Body022,Body023,Body025]
  Type = 0
  X = 0
  XDirection = (1,0,0)
  Y = 0
FEATURE [TechDraw::DrawProjGroup] ProjGroup015
  Anchor = -> ProjItem018
  AutoDistribute = true
  LockPosition = false
  ProjectionType = 0
  Rotation = 0
  ScaleType = 0
  Source = -> [Body,Body021,Body022,Body023,Body025]
  Views = -> [ProjItem018]
  X = 105
  Y = 148.5
  spacingX = 15
  spacingY = 15
FEATURE [TechDraw::DrawViewDimension] Dimension125
  Arbitrary = false
  ArbitraryTolerances = false
  EqualTolerance = true
  FormatSpec = %.2f
  FormatSpecOverTolerance = %+.2f
  FormatSpecUnderTolerance = %+.2f
  Inverted = false
  LockPosition = false
  MeasureType = 1
  OverTolerance = 0
  References2D = -> [ProjItem018]
  Rotation = 0
  ScaleType = 0
  TheoreticalExact = false
  Type = 1
  UnderTolerance = 0
  X = -1.63187
  Y = -83.5989
FEATURE [TechDraw::DrawViewDimension] Dimension126
  Arbitrary = false
  ArbitraryTolerances = false
  EqualTolerance = true
  FormatSpec = %.2f
  FormatSpecOverTolerance = %+.2f
  FormatSpecUnderTolerance = %+.2f
  Inverted = false
  LockPosition = false
  MeasureType = 1
  OverTolerance = 0
  References2D = -> [ProjItem018]
  Rotation = 0
  ScaleType = 0
  TheoreticalExact = false
  Type = 1
  UnderTolerance = 0
  X = -71.6813
  Y = 80
FEATURE [TechDraw::DrawViewDimension] Dimension127
  Arbitrary = false
  ArbitraryTolerances = false
  EqualTolerance = true
  FormatSpec = %.2f
  FormatSpecOverTolerance = %+.2f
  FormatSpecUnderTolerance = %+.2f
  Inverted = false
  LockPosition = false
  MeasureType = 1
  OverTolerance = 0
  References2D = -> [ProjItem018]
  Rotation = 0
  ScaleType = 0
  TheoreticalExact = false
  Type = 2
  UnderTolerance = 0
  X = -59.0604
  Y = 95.7747
FEATURE [TechDraw::DrawViewDimension] Dimension128
  Arbitrary = false
  ArbitraryTolerances = false
  EqualTolerance = true
  FormatSpec = %.2f
  FormatSpecOverTolerance = %+.2f
  FormatSpecUnderTolerance = %+.2f
  Inverted = false
  LockPosition = false
  MeasureType = 1
  OverTolerance = 0
  References2D = -> [ProjItem018]
  Rotation = 0
  ScaleType = 0
  TheoreticalExact = false
  Type = 2
  UnderTolerance = 0
  X = 77.3022
  Y = 74.7747
FEATURE [TechDraw::DrawViewDimension] Dimension129
  Arbitrary = false
  ArbitraryTolerances = false
  EqualTolerance = true
  FormatSpec = %.2f
  FormatSpecOverTolerance = %+.2f
  FormatSpecUnderTolerance = %+.2f
  Inverted = false
  LockPosition = false
  MeasureType = 1
  OverTolerance = 0
  References2D = -> [ProjItem018]
  Rotation = 0
  ScaleType = 0
  TheoreticalExact = false
  Type = 2
  UnderTolerance = 0
  X = -57.3571
  Y = -92.5769
FEATURE [TechDraw::DrawViewDimension] Dimension130
  Arbitrary = false
  ArbitraryTolerances = false
  EqualTolerance = true
  FormatSpec = %.2f
  FormatSpecOverTolerance = %+.2f
  FormatSpecUnderTolerance = %+.2f
  Inverted = false
  LockPosition = false
  MeasureType = 1
  OverTolerance = 0
  References2D = -> [ProjItem018]
  Rotation = 0
  ScaleType = 0
  TheoreticalExact = false
  Type = 1
  UnderTolerance = 0
  X = 55.3242
  Y = -63.8407
FEATURE [TechDraw::DrawViewDimension] Dimension131
  Arbitrary = false
  ArbitraryTolerances = false
  EqualTolerance = true
  FormatSpec = %.2f
  FormatSpecOverTolerance = %+.2f
  FormatSpecUnderTolerance = %+.2f
  Inverted = false
  LockPosition = false
  MeasureType = 1
  OverTolerance = 0
  References2D = -> [ProjItem018]
  Rotation = 0
  ScaleType = 0
  TheoreticalExact = false
  Type = 1
  UnderTolerance = 0
  X = 48.8681
  Y = -53.3242
FEATURE [TechDraw::DrawViewDimension] Dimension132
  Arbitrary = false
  ArbitraryTolerances = false
  EqualTolerance = true
  FormatSpec = ⌀%.2f
  FormatSpecOverTolerance = %+.2f
  FormatSpecUnderTolerance = %+.2f
  Inverted = false
  LockPosition = false
  MeasureType = 1
  OverTolerance = 0
  References2D = -> [ProjItem018]
  Rotation = 0
  ScaleType = 0
  TheoreticalExact = false
  Type = 5
  UnderTolerance = 0
  X = 43.3352
  Y = 96.4615
FEATURE [TechDraw::DrawViewDimension] Dimension133
  Arbitrary = false
  ArbitraryTolerances = false
  EqualTolerance = true
  FormatSpec = ⌀%.2f
  FormatSpecOverTolerance = %+.2f
  FormatSpecUnderTolerance = %+.2f
  Inverted = false
  LockPosition = false
  MeasureType = 1
  OverTolerance = 0
  References2D = -> [ProjItem018]
  Rotation = 0
  ScaleType = 0
  TheoreticalExact = false
  Type = 5
  UnderTolerance = 0
  X = 6.34615
  Y = -50.9505
FEATURE [TechDraw::DrawPage] Page006
  KeepUpdated = true
  NextBalloonIndex = 1
  ProjectionType = 0
  Template = -> Template006
  Views = -> [ProjGroup015,Dimension125,Dimension126,Dimension127,Dimension128,Dimension129,Dimension130,Dimension131,Dimension132,Dimension133]
